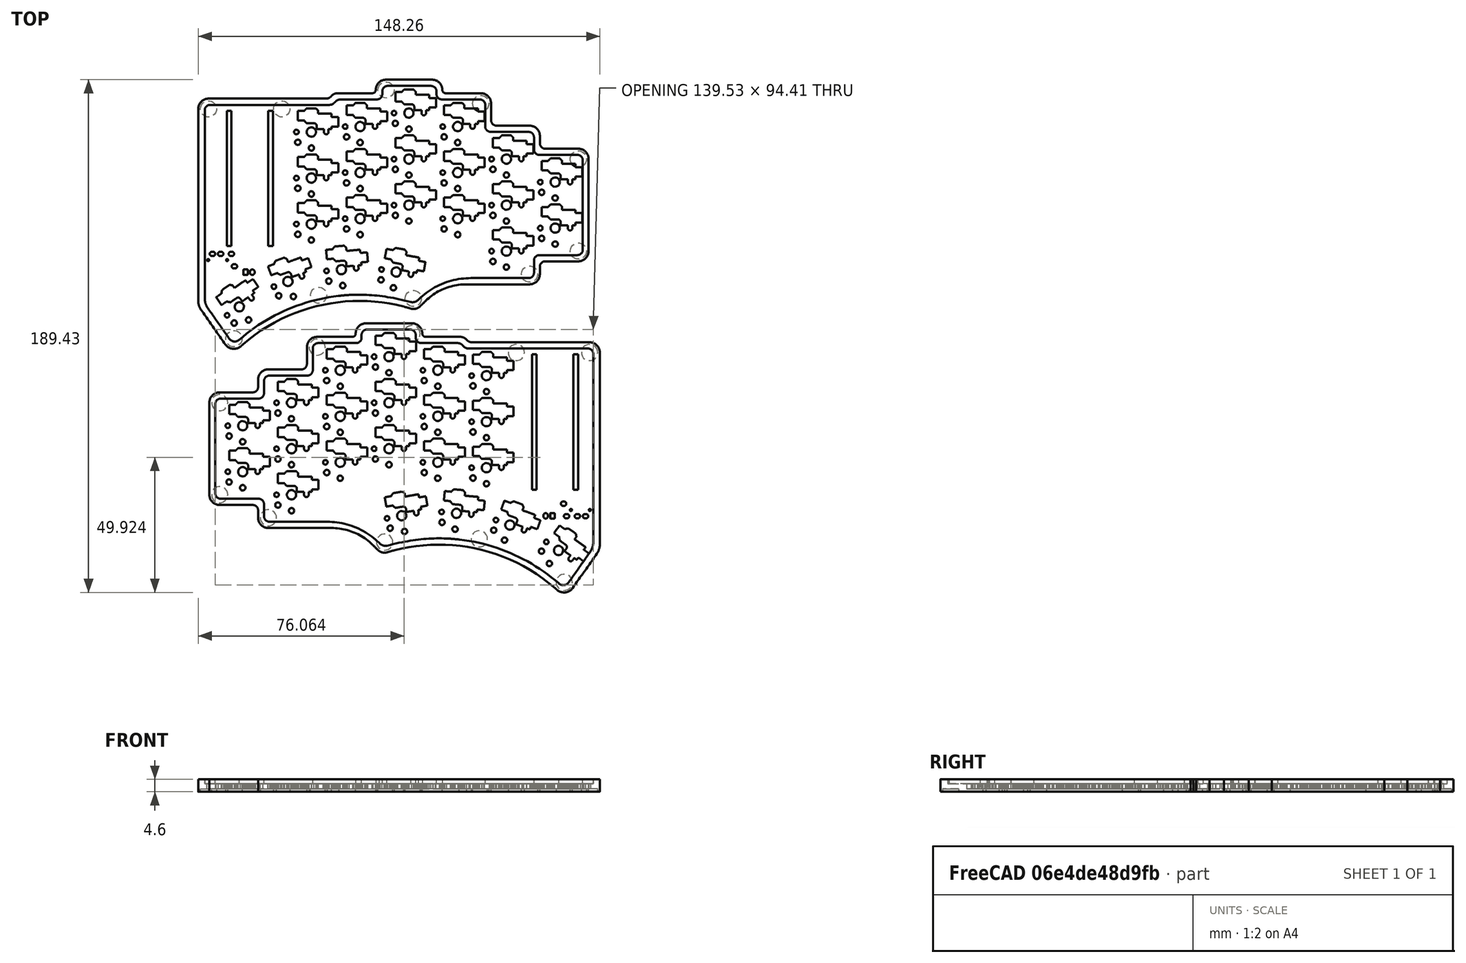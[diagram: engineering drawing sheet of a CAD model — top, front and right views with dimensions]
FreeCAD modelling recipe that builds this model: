
FCSTD DOCUMENT  (FreeCAD 0.21R33771 (Git))
Label: case_simple
License: All rights reserved
LicenseURL: http://en.wikipedia.org/wiki/All_rights_reserved
objects: Part::Feature×242, Part::Extrusion×242, Part::FeaturePython×5, Part::MultiFuse×3, Part::Mirroring×1
note: 493 computed .brp shape members not serialized (recipe doc carries the construction recipe); baked Part::Feature solids carry a one-line shape summary decoded from their .brp

FEATURE [Part::Feature] path44149_5_3
  shape: bbox 144.1 x 99.92 x 2e-07 mm, 0 faces, 0 solids (baked)
FEATURE [Part::Extrusion] Extrude  label="bounds"
  Base = -> path44149_5_3
  Dir = (0,0,1)
  DirMode = 0
  FaceMakerClass = Part::FaceMakerBullseye
  LengthFwd = 4.6
  LengthRev = 0
  Solid = true
  Symmetric = false
FEATURE [Part::Feature] path9
  Placement = pos=(72.4721,-86.7664,0) rot=(0,0,1;0rad)
  shape: bbox 6.624 x 7.244 x 2e-07 mm, 0 faces, 0 solids (baked)
FEATURE [Part::Feature] path9_9
  Placement = pos=(72.4721,-120.766,0) rot=(0,0,1;0rad)
  shape: bbox 6.624 x 7.244 x 2e-07 mm, 0 faces, 0 solids (baked)
FEATURE [Part::Feature] path9_92_7_9_8
  Placement = pos=(108.472,-66.2664,0) rot=(0,0,1;0rad)
  shape: bbox 6.624 x 7.244 x 2e-07 mm, 0 faces, 0 solids (baked)
FEATURE [Part::Feature] path9_92_7_9_9
  Placement = pos=(143.472,-61.2664,0) rot=(0,0,1;0rad)
  shape: bbox 6.624 x 7.244 x 2e-07 mm, 0 faces, 0 solids (baked)
FEATURE [Part::Feature] path9_92_7_9_9_4
  Placement = pos=(209.001,-68.2664,0) rot=(0,0,1;0rad)
  shape: bbox 6.624 x 7.244 x 2e-07 mm, 0 faces, 0 solids (baked)
FEATURE [Part::Feature] path9_9_5
  Placement = pos=(90.4721,-129.266,0) rot=(0,0,1;0rad)
  shape: bbox 6.624 x 7.244 x 2e-07 mm, 0 faces, 0 solids (baked)
FEATURE [Part::Feature] path9_92_7_9_9_4_4_8_2
  Placement = pos=(199.634,-153.132,0) rot=(0,0,1;0rad)
  shape: bbox 6.624 x 7.244 x 2e-07 mm, 0 faces, 0 solids (baked)
FEATURE [Part::Feature] path9_92_7_9_9_4_4_8_2_4
  Placement = pos=(133.404,-138.274,0) rot=(0,0,1;0rad)
  shape: bbox 6.624 x 7.244 x 2e-07 mm, 0 faces, 0 solids (baked)
FEATURE [Part::Feature] path9_92_7_9_9_4_4_8_2_4_6
  Placement = pos=(168.299,-137.096,0) rot=(0,0,1;0rad)
  shape: bbox 6.624 x 7.244 x 2e-07 mm, 0 faces, 0 solids (baked)
FEATURE [Part::Feature] path9_92_7_9_9_4_4_8_2_4_0
  Placement = pos=(181.972,-68.2664,0) rot=(0,0,1;0rad)
  shape: bbox 6.624 x 7.244 x 2e-07 mm, 0 faces, 0 solids (baked)
FEATURE [Part::Extrusion] Extrude001
  Base = -> path9
  Dir = (0,0,1)
  DirMode = 0
  FaceMakerClass = Part::FaceMakerBullseye
  LengthFwd = 1
  LengthRev = 0
  Solid = true
  Symmetric = false
FEATURE [Part::Extrusion] Extrude002
  Base = -> path9_9
  Dir = (0,0,1)
  DirMode = 0
  FaceMakerClass = Part::FaceMakerBullseye
  LengthFwd = 1
  LengthRev = 0
  Solid = true
  Symmetric = false
FEATURE [Part::Extrusion] Extrude003
  Base = -> path9_92_7_9_8
  Dir = (0,0,1)
  DirMode = 0
  FaceMakerClass = Part::FaceMakerBullseye
  LengthFwd = 1
  LengthRev = 0
  Solid = true
  Symmetric = false
FEATURE [Part::Extrusion] Extrude004
  Base = -> path9_92_7_9_9
  Dir = (0,0,1)
  DirMode = 0
  FaceMakerClass = Part::FaceMakerBullseye
  LengthFwd = 1
  LengthRev = 0
  Solid = true
  Symmetric = false
FEATURE [Part::Extrusion] Extrude005
  Base = -> path9_92_7_9_9_4
  Dir = (0,0,1)
  DirMode = 0
  FaceMakerClass = Part::FaceMakerBullseye
  LengthFwd = 1
  LengthRev = 0
  Solid = true
  Symmetric = false
FEATURE [Part::Extrusion] Extrude006
  Base = -> path9_9_5
  Dir = (0,0,1)
  DirMode = 0
  FaceMakerClass = Part::FaceMakerBullseye
  LengthFwd = 1
  LengthRev = 0
  Solid = true
  Symmetric = false
FEATURE [Part::Extrusion] Extrude007
  Base = -> path9_92_7_9_9_4_4_8_2
  Dir = (0,0,1)
  DirMode = 0
  FaceMakerClass = Part::FaceMakerBullseye
  LengthFwd = 1
  LengthRev = 0
  Solid = true
  Symmetric = false
FEATURE [Part::Extrusion] Extrude008
  Base = -> path9_92_7_9_9_4_4_8_2_4
  Dir = (0,0,1)
  DirMode = 0
  FaceMakerClass = Part::FaceMakerBullseye
  LengthFwd = 1
  LengthRev = 0
  Solid = true
  Symmetric = false
FEATURE [Part::Extrusion] Extrude009
  Base = -> path9_92_7_9_9_4_4_8_2_4_6
  Dir = (0,0,1)
  DirMode = 0
  FaceMakerClass = Part::FaceMakerBullseye
  LengthFwd = 1
  LengthRev = 0
  Solid = true
  Symmetric = false
FEATURE [Part::Extrusion] Extrude010
  Base = -> path9_92_7_9_9_4_4_8_2_4_0
  Dir = (0,0,1)
  DirMode = 0
  FaceMakerClass = Part::FaceMakerBullseye
  LengthFwd = 1
  LengthRev = 0
  Solid = true
  Symmetric = false
FEATURE [Part::MultiFuse] Fusion  label="feet"
  Shapes = -> [Extrude010,Extrude001,Extrude002,Extrude003,Extrude004,Extrude005,Extrude006,Extrude007,Extrude008,Extrude009]
FEATURE [Part::Feature] path52377_0_5_0_4_2_41_0_0_5_6
  shape: bbox 15 x 9.586 x 2e-07 mm, 0 faces, 0 solids (baked)
FEATURE [Part::Feature] path34096_2_0
  Placement = pos=(15.9497,-145.166,0) rot=(0,0,1;0rad)
  shape: bbox 2.208 x 2.415 x 2e-07 mm, 0 faces, 0 solids (baked)
FEATURE [Part::Feature] path34096_9
  Placement = pos=(20.9497,-147.266,0) rot=(0,0,1;0rad)
  shape: bbox 2.208 x 2.415 x 2e-07 mm, 0 faces, 0 solids (baked)
FEATURE [Part::Feature] path34072_1_9
  Placement = pos=(15.4497,-141.366,0) rot=(0,0,1;0rad)
  shape: bbox 1.877 x 2.052 x 2e-07 mm, 0 faces, 0 solids (baked)
FEATURE [Part::Feature] path34070_8
  Placement = pos=(20.9497,-141.366,0) rot=(0,0,1;0rad)
  shape: bbox 3.787 x 4.141 x 2e-07 mm, 0 faces, 0 solids (baked)
FEATURE [Part::Feature] path52377_0_5_0_4_2_41_0_0_5_6_5
  shape: bbox 15 x 9.586 x 2e-07 mm, 0 faces, 0 solids (baked)
FEATURE [Part::Feature] path34096_2_0_4
  Placement = pos=(15.9497,-145.166,0) rot=(0,0,1;0rad)
  shape: bbox 2.208 x 2.415 x 2e-07 mm, 0 faces, 0 solids (baked)
FEATURE [Part::Feature] path34096_9_4
  Placement = pos=(20.9497,-147.266,0) rot=(0,0,1;0rad)
  shape: bbox 2.208 x 2.415 x 2e-07 mm, 0 faces, 0 solids (baked)
FEATURE [Part::Feature] path34072_1_9_5
  Placement = pos=(15.4497,-141.366,0) rot=(0,0,1;0rad)
  shape: bbox 1.877 x 2.052 x 2e-07 mm, 0 faces, 0 solids (baked)
FEATURE [Part::Feature] path34070_8_0
  Placement = pos=(20.9497,-141.366,0) rot=(0,0,1;0rad)
  shape: bbox 3.787 x 4.141 x 2e-07 mm, 0 faces, 0 solids (baked)
FEATURE [Part::Feature] path52377_0_5_0_4_2_41_0_0_5_6_1
  shape: bbox 15 x 9.586 x 2e-07 mm, 0 faces, 0 solids (baked)
FEATURE [Part::Feature] path34096_2_0_0
  Placement = pos=(15.9497,-145.166,0) rot=(0,0,1;0rad)
  shape: bbox 2.208 x 2.415 x 2e-07 mm, 0 faces, 0 solids (baked)
FEATURE [Part::Feature] path34096_9_5
  Placement = pos=(20.9497,-147.266,0) rot=(0,0,1;0rad)
  shape: bbox 2.208 x 2.415 x 2e-07 mm, 0 faces, 0 solids (baked)
FEATURE [Part::Feature] path34072_1_9_51
  Placement = pos=(15.4497,-141.366,0) rot=(0,0,1;0rad)
  shape: bbox 1.877 x 2.052 x 2e-07 mm, 0 faces, 0 solids (baked)
FEATURE [Part::Feature] path34070_8_4
  Placement = pos=(20.9497,-141.366,0) rot=(0,0,1;0rad)
  shape: bbox 3.787 x 4.141 x 2e-07 mm, 0 faces, 0 solids (baked)
FEATURE [Part::Feature] path52377_0_5_0_4_2_41_0_0_5_6_1_6
  shape: bbox 15 x 9.586 x 2e-07 mm, 0 faces, 0 solids (baked)
FEATURE [Part::Feature] path34096_2_0_0_2
  Placement = pos=(15.9497,-145.166,0) rot=(0,0,1;0rad)
  shape: bbox 2.208 x 2.415 x 2e-07 mm, 0 faces, 0 solids (baked)
FEATURE [Part::Feature] path34096_9_5_7
  Placement = pos=(20.9497,-147.266,0) rot=(0,0,1;0rad)
  shape: bbox 2.208 x 2.415 x 2e-07 mm, 0 faces, 0 solids (baked)
FEATURE [Part::Feature] path34072_1_9_51_2
  Placement = pos=(15.4497,-141.366,0) rot=(0,0,1;0rad)
  shape: bbox 1.877 x 2.052 x 2e-07 mm, 0 faces, 0 solids (baked)
FEATURE [Part::Feature] path34070_8_4_6
  Placement = pos=(20.9497,-141.366,0) rot=(0,0,1;0rad)
  shape: bbox 3.787 x 4.141 x 2e-07 mm, 0 faces, 0 solids (baked)
FEATURE [Part::Feature] path52377_0_5_0_4_2_41_0_0_5_6_5_7
  shape: bbox 15 x 9.586 x 2e-07 mm, 0 faces, 0 solids (baked)
FEATURE [Part::Feature] path34096_2_0_4_8
  Placement = pos=(15.9497,-145.166,0) rot=(0,0,1;0rad)
  shape: bbox 2.208 x 2.415 x 2e-07 mm, 0 faces, 0 solids (baked)
FEATURE [Part::Feature] path34096_9_4_8
  Placement = pos=(20.9497,-147.266,0) rot=(0,0,1;0rad)
  shape: bbox 2.208 x 2.415 x 2e-07 mm, 0 faces, 0 solids (baked)
FEATURE [Part::Feature] path34072_1_9_5_5
  Placement = pos=(15.4497,-141.366,0) rot=(0,0,1;0rad)
  shape: bbox 1.877 x 2.052 x 2e-07 mm, 0 faces, 0 solids (baked)
FEATURE [Part::Feature] path34070_8_0_8
  Placement = pos=(20.9497,-141.366,0) rot=(0,0,1;0rad)
  shape: bbox 3.787 x 4.141 x 2e-07 mm, 0 faces, 0 solids (baked)
FEATURE [Part::Feature] path52377_0_5_0_4_2_41_0_0_5_6_1_7
  shape: bbox 15 x 9.586 x 2e-07 mm, 0 faces, 0 solids (baked)
FEATURE [Part::Feature] path34096_2_0_0_4
  Placement = pos=(15.9497,-145.166,0) rot=(0,0,1;0rad)
  shape: bbox 2.208 x 2.415 x 2e-07 mm, 0 faces, 0 solids (baked)
FEATURE [Part::Feature] path34096_9_5_75
  Placement = pos=(20.9497,-147.266,0) rot=(0,0,1;0rad)
  shape: bbox 2.208 x 2.415 x 2e-07 mm, 0 faces, 0 solids (baked)
FEATURE [Part::Feature] path34072_1_9_51_8
  Placement = pos=(15.4497,-141.366,0) rot=(0,0,1;0rad)
  shape: bbox 1.877 x 2.052 x 2e-07 mm, 0 faces, 0 solids (baked)
FEATURE [Part::Feature] path34070_8_4_65
  Placement = pos=(20.9497,-141.366,0) rot=(0,0,1;0rad)
  shape: bbox 3.787 x 4.141 x 2e-07 mm, 0 faces, 0 solids (baked)
FEATURE [Part::Feature] path52377_0_5_0_4_2_41_0_0_5_6_1_6_5
  shape: bbox 15 x 9.586 x 2e-07 mm, 0 faces, 0 solids (baked)
FEATURE [Part::Feature] path34096_2_0_0_2_7
  Placement = pos=(15.9497,-145.166,0) rot=(0,0,1;0rad)
  shape: bbox 2.208 x 2.415 x 2e-07 mm, 0 faces, 0 solids (baked)
FEATURE [Part::Feature] path34096_9_5_7_9
  Placement = pos=(20.9497,-147.266,0) rot=(0,0,1;0rad)
  shape: bbox 2.208 x 2.415 x 2e-07 mm, 0 faces, 0 solids (baked)
FEATURE [Part::Feature] path34072_1_9_51_2_1
  Placement = pos=(15.4497,-141.366,0) rot=(0,0,1;0rad)
  shape: bbox 1.877 x 2.052 x 2e-07 mm, 0 faces, 0 solids (baked)
FEATURE [Part::Feature] path34070_8_4_6_1
  Placement = pos=(20.9497,-141.366,0) rot=(0,0,1;0rad)
  shape: bbox 3.787 x 4.141 x 2e-07 mm, 0 faces, 0 solids (baked)
FEATURE [Part::Feature] path52377_0_5_0_4_2_41_0_0_5_6_5_7_1
  shape: bbox 15 x 9.586 x 2e-07 mm, 0 faces, 0 solids (baked)
FEATURE [Part::Feature] path34096_2_0_4_8_5
  Placement = pos=(15.9497,-145.166,0) rot=(0,0,1;0rad)
  shape: bbox 2.208 x 2.415 x 2e-07 mm, 0 faces, 0 solids (baked)
FEATURE [Part::Feature] path34096_9_4_8_5
  Placement = pos=(20.9497,-147.266,0) rot=(0,0,1;0rad)
  shape: bbox 2.208 x 2.415 x 2e-07 mm, 0 faces, 0 solids (baked)
FEATURE [Part::Feature] path34072_1_9_5_5_4
  Placement = pos=(15.4497,-141.366,0) rot=(0,0,1;0rad)
  shape: bbox 1.877 x 2.052 x 2e-07 mm, 0 faces, 0 solids (baked)
FEATURE [Part::Feature] path34070_8_0_8_3
  Placement = pos=(20.9497,-141.366,0) rot=(0,0,1;0rad)
  shape: bbox 3.787 x 4.141 x 2e-07 mm, 0 faces, 0 solids (baked)
FEATURE [Part::Feature] path52377_0_5_0_4_2_41_0_0_5_6_1_7_8
  shape: bbox 15 x 9.586 x 2e-07 mm, 0 faces, 0 solids (baked)
FEATURE [Part::Feature] path34096_2_0_0_4_5
  Placement = pos=(15.9497,-145.166,0) rot=(0,0,1;0rad)
  shape: bbox 2.208 x 2.415 x 2e-07 mm, 0 faces, 0 solids (baked)
FEATURE [Part::Feature] path34096_9_5_75_5
  Placement = pos=(20.9497,-147.266,0) rot=(0,0,1;0rad)
  shape: bbox 2.208 x 2.415 x 2e-07 mm, 0 faces, 0 solids (baked)
FEATURE [Part::Feature] path34072_1_9_51_8_1
  Placement = pos=(15.4497,-141.366,0) rot=(0,0,1;0rad)
  shape: bbox 1.877 x 2.052 x 2e-07 mm, 0 faces, 0 solids (baked)
FEATURE [Part::Feature] path34070_8_4_65_1
  Placement = pos=(20.9497,-141.366,0) rot=(0,0,1;0rad)
  shape: bbox 3.787 x 4.141 x 2e-07 mm, 0 faces, 0 solids (baked)
FEATURE [Part::Feature] path52377_0_5_0_4_2_41_0_0_5_6_1_6_5_2
  shape: bbox 15 x 9.586 x 2e-07 mm, 0 faces, 0 solids (baked)
FEATURE [Part::Feature] path34096_2_0_0_2_7_9
  Placement = pos=(15.9497,-145.166,0) rot=(0,0,1;0rad)
  shape: bbox 2.208 x 2.415 x 2e-07 mm, 0 faces, 0 solids (baked)
FEATURE [Part::Feature] path34096_9_5_7_9_4
  Placement = pos=(20.9497,-147.266,0) rot=(0,0,1;0rad)
  shape: bbox 2.208 x 2.415 x 2e-07 mm, 0 faces, 0 solids (baked)
FEATURE [Part::Feature] path34072_1_9_51_2_1_3
  Placement = pos=(15.4497,-141.366,0) rot=(0,0,1;0rad)
  shape: bbox 1.877 x 2.052 x 2e-07 mm, 0 faces, 0 solids (baked)
FEATURE [Part::Feature] path34070_8_4_6_1_4
  Placement = pos=(20.9497,-141.366,0) rot=(0,0,1;0rad)
  shape: bbox 3.787 x 4.141 x 2e-07 mm, 0 faces, 0 solids (baked)
FEATURE [Part::Feature] path52377_0_5_0_4_2_41_0_0_5_6_5_7_1_6
  shape: bbox 15 x 9.586 x 2e-07 mm, 0 faces, 0 solids (baked)
FEATURE [Part::Feature] path34096_2_0_4_8_5_4
  Placement = pos=(15.9497,-145.166,0) rot=(0,0,1;0rad)
  shape: bbox 2.208 x 2.415 x 2e-07 mm, 0 faces, 0 solids (baked)
FEATURE [Part::Feature] path34096_9_4_8_5_3
  Placement = pos=(20.9497,-147.266,0) rot=(0,0,1;0rad)
  shape: bbox 2.208 x 2.415 x 2e-07 mm, 0 faces, 0 solids (baked)
FEATURE [Part::Feature] path34072_1_9_5_5_4_4
  Placement = pos=(15.4497,-141.366,0) rot=(0,0,1;0rad)
  shape: bbox 1.877 x 2.052 x 2e-07 mm, 0 faces, 0 solids (baked)
FEATURE [Part::Feature] path34070_8_0_8_3_3
  Placement = pos=(20.9497,-141.366,0) rot=(0,0,1;0rad)
  shape: bbox 3.787 x 4.141 x 2e-07 mm, 0 faces, 0 solids (baked)
FEATURE [Part::Feature] path52377_0_5_0_4_2_41_0_0_5_6_1_7_9
  shape: bbox 15 x 9.586 x 2e-07 mm, 0 faces, 0 solids (baked)
FEATURE [Part::Feature] path34096_2_0_0_4_52
  Placement = pos=(15.9497,-145.166,0) rot=(0,0,1;0rad)
  shape: bbox 2.208 x 2.415 x 2e-07 mm, 0 faces, 0 solids (baked)
FEATURE [Part::Feature] path34096_9_5_75_2
  Placement = pos=(20.9497,-147.266,0) rot=(0,0,1;0rad)
  shape: bbox 2.208 x 2.415 x 2e-07 mm, 0 faces, 0 solids (baked)
FEATURE [Part::Feature] path34072_1_9_51_8_2
  Placement = pos=(15.4497,-141.366,0) rot=(0,0,1;0rad)
  shape: bbox 1.877 x 2.052 x 2e-07 mm, 0 faces, 0 solids (baked)
FEATURE [Part::Feature] path34070_8_4_65_5
  Placement = pos=(20.9497,-141.366,0) rot=(0,0,1;0rad)
  shape: bbox 3.787 x 4.141 x 2e-07 mm, 0 faces, 0 solids (baked)
FEATURE [Part::Feature] path52377_0_5_0_4_2_41_0_0_5_6_1_6_5_3
  shape: bbox 15 x 9.586 x 2e-07 mm, 0 faces, 0 solids (baked)
FEATURE [Part::Feature] path34096_2_0_0_2_7_3
  Placement = pos=(15.9497,-145.166,0) rot=(0,0,1;0rad)
  shape: bbox 2.208 x 2.415 x 2e-07 mm, 0 faces, 0 solids (baked)
FEATURE [Part::Feature] path34096_9_5_7_9_0
  Placement = pos=(20.9497,-147.266,0) rot=(0,0,1;0rad)
  shape: bbox 2.208 x 2.415 x 2e-07 mm, 0 faces, 0 solids (baked)
FEATURE [Part::Feature] path34072_1_9_51_2_1_9
  Placement = pos=(15.4497,-141.366,0) rot=(0,0,1;0rad)
  shape: bbox 1.877 x 2.052 x 2e-07 mm, 0 faces, 0 solids (baked)
FEATURE [Part::Feature] path34070_8_4_6_1_5
  Placement = pos=(20.9497,-141.366,0) rot=(0,0,1;0rad)
  shape: bbox 3.787 x 4.141 x 2e-07 mm, 0 faces, 0 solids (baked)
FEATURE [Part::Feature] path52377_0_5_0_4_2_41_0_0_5_6_5_7_1_9
  shape: bbox 15 x 9.586 x 2e-07 mm, 0 faces, 0 solids (baked)
FEATURE [Part::Feature] path34096_2_0_4_8_5_1
  Placement = pos=(15.9497,-145.166,0) rot=(0,0,1;0rad)
  shape: bbox 2.208 x 2.415 x 2e-07 mm, 0 faces, 0 solids (baked)
FEATURE [Part::Feature] path34096_9_4_8_5_9
  Placement = pos=(20.9497,-147.266,0) rot=(0,0,1;0rad)
  shape: bbox 2.208 x 2.415 x 2e-07 mm, 0 faces, 0 solids (baked)
FEATURE [Part::Feature] path34072_1_9_5_5_4_3
  Placement = pos=(15.4497,-141.366,0) rot=(0,0,1;0rad)
  shape: bbox 1.877 x 2.052 x 2e-07 mm, 0 faces, 0 solids (baked)
FEATURE [Part::Feature] path34070_8_0_8_3_8
  Placement = pos=(20.9497,-141.366,0) rot=(0,0,1;0rad)
  shape: bbox 3.787 x 4.141 x 2e-07 mm, 0 faces, 0 solids (baked)
FEATURE [Part::Feature] path52377_0_5_0_4_2_41_0_0_5_6_5_7_1_9_7
  shape: bbox 15.77 x 8.879 x 2e-07 mm, 0 faces, 0 solids (baked)
FEATURE [Part::Feature] path34096_2_0_4_8_5_1_5
  Placement = pos=(15.9497,-145.166,0) rot=(0,0,1;0rad)
  shape: bbox 2.386 x 2.384 x 2e-07 mm, 0 faces, 0 solids (baked)
FEATURE [Part::Feature] path34096_9_4_8_5_9_9
  Placement = pos=(20.9497,-147.266,0) rot=(0,0,1;0rad)
  shape: bbox 2.386 x 2.384 x 2e-07 mm, 0 faces, 0 solids (baked)
FEATURE [Part::Feature] path34072_1_9_5_5_4_3_4
  Placement = pos=(15.4497,-141.366,0) rot=(0,0,1;0rad)
  shape: bbox 2.028 x 2.027 x 2e-07 mm, 0 faces, 0 solids (baked)
FEATURE [Part::Feature] path34070_8_0_8_3_8_5
  Placement = pos=(20.9497,-141.366,0) rot=(0,0,1;0rad)
  shape: bbox 4.091 x 4.089 x 2e-07 mm, 0 faces, 0 solids (baked)
FEATURE [Part::Feature] path52377_0_5_0_4_2_41_0_0_5_6_5_7_1_9_7_1
  shape: bbox 15.05 x 10.25 x 2e-07 mm, 0 faces, 0 solids (baked)
FEATURE [Part::Feature] path34096_2_0_4_8_5_1_5_0
  Placement = pos=(15.9497,-145.166,0) rot=(0,0,1;0rad)
  shape: bbox 2.351 x 2.407 x 2e-07 mm, 0 faces, 0 solids (baked)
FEATURE [Part::Feature] path34096_9_4_8_5_9_9_0
  Placement = pos=(20.9497,-147.266,0) rot=(0,0,1;0rad)
  shape: bbox 2.351 x 2.407 x 2e-07 mm, 0 faces, 0 solids (baked)
FEATURE [Part::Feature] path34072_1_9_5_5_4_3_4_2
  Placement = pos=(15.4497,-141.366,0) rot=(0,0,1;0rad)
  shape: bbox 1.999 x 2.046 x 2e-07 mm, 0 faces, 0 solids (baked)
FEATURE [Part::Feature] path34070_8_0_8_3_8_5_0
  Placement = pos=(20.9497,-141.366,0) rot=(0,0,1;0rad)
  shape: bbox 4.033 x 4.128 x 2e-07 mm, 0 faces, 0 solids (baked)
FEATURE [Part::Feature] path52377_0_5_0_4_2_41_0_0_5_6_5_7_1_9_7_1_9
  shape: bbox 14.52 x 11.86 x 2e-07 mm, 0 faces, 0 solids (baked)
FEATURE [Part::Feature] path34096_2_0_4_8_5_1_5_0_3
  Placement = pos=(15.9497,-145.166,0) rot=(0,0,1;0rad)
  shape: bbox 2.384 x 2.386 x 2e-07 mm, 0 faces, 0 solids (baked)
FEATURE [Part::Feature] path34096_9_4_8_5_9_9_0_4
  Placement = pos=(20.9497,-147.266,0) rot=(0,0,1;0rad)
  shape: bbox 2.384 x 2.386 x 2e-07 mm, 0 faces, 0 solids (baked)
FEATURE [Part::Feature] path34072_1_9_5_5_4_3_4_2_6
  Placement = pos=(15.4497,-141.366,0) rot=(0,0,1;0rad)
  shape: bbox 2.027 x 2.028 x 2e-07 mm, 0 faces, 0 solids (baked)
FEATURE [Part::Feature] path34070_8_0_8_3_8_5_0_4
  Placement = pos=(20.9497,-141.366,0) rot=(0,0,1;0rad)
  shape: bbox 4.089 x 4.091 x 2e-07 mm, 0 faces, 0 solids (baked)
FEATURE [Part::Feature] path52377_0_5_0_4_2_41_0_0_5_6_5_7_1_9_7_1_1
  shape: bbox 13 x 13.34 x 2e-07 mm, 0 faces, 0 solids (baked)
FEATURE [Part::Feature] path34096_2_0_4_8_5_1_5_0_5
  Placement = pos=(15.9497,-145.166,0) rot=(0,0,1;0rad)
  shape: bbox 2.407 x 2.351 x 2e-07 mm, 0 faces, 0 solids (baked)
FEATURE [Part::Feature] path34096_9_4_8_5_9_9_0_8
  Placement = pos=(20.9497,-147.266,0) rot=(0,0,1;0rad)
  shape: bbox 2.407 x 2.351 x 2e-07 mm, 0 faces, 0 solids (baked)
FEATURE [Part::Feature] path34072_1_9_5_5_4_3_4_2_3
  Placement = pos=(15.4497,-141.366,0) rot=(0,0,1;0rad)
  shape: bbox 2.046 x 1.999 x 2e-07 mm, 0 faces, 0 solids (baked)
FEATURE [Part::Feature] path34070_8_0_8_3_8_5_0_7
  Placement = pos=(20.9497,-141.366,0) rot=(0,0,1;0rad)
  shape: bbox 4.128 x 4.033 x 2e-07 mm, 0 faces, 0 solids (baked)
FEATURE [Part::Feature] path52377_0_5_0_4_2_41_0_0_5_6_1_7_0
  shape: bbox 15 x 9.586 x 2e-07 mm, 0 faces, 0 solids (baked)
FEATURE [Part::Feature] path34096_2_0_0_4_9
  Placement = pos=(15.9497,-145.166,0) rot=(0,0,1;0rad)
  shape: bbox 2.208 x 2.415 x 2e-07 mm, 0 faces, 0 solids (baked)
FEATURE [Part::Feature] path34096_9_5_75_3
  Placement = pos=(20.9497,-147.266,0) rot=(0,0,1;0rad)
  shape: bbox 2.208 x 2.415 x 2e-07 mm, 0 faces, 0 solids (baked)
FEATURE [Part::Feature] path34072_1_9_51_8_3
  Placement = pos=(15.4497,-141.366,0) rot=(0,0,1;0rad)
  shape: bbox 1.877 x 2.052 x 2e-07 mm, 0 faces, 0 solids (baked)
FEATURE [Part::Feature] path34070_8_4_65_6
  Placement = pos=(20.9497,-141.366,0) rot=(0,0,1;0rad)
  shape: bbox 3.787 x 4.141 x 2e-07 mm, 0 faces, 0 solids (baked)
FEATURE [Part::Feature] path52377_0_5_0_4_2_41_0_0_5_6_1_6_5_0
  shape: bbox 15 x 9.586 x 2e-07 mm, 0 faces, 0 solids (baked)
FEATURE [Part::Feature] path34096_2_0_0_2_7_5
  Placement = pos=(15.9497,-145.166,0) rot=(0,0,1;0rad)
  shape: bbox 2.208 x 2.415 x 2e-07 mm, 0 faces, 0 solids (baked)
FEATURE [Part::Feature] path34096_9_5_7_9_2
  Placement = pos=(20.9497,-147.266,0) rot=(0,0,1;0rad)
  shape: bbox 2.208 x 2.415 x 2e-07 mm, 0 faces, 0 solids (baked)
FEATURE [Part::Feature] path34072_1_9_51_2_1_4
  Placement = pos=(15.4497,-141.366,0) rot=(0,0,1;0rad)
  shape: bbox 1.877 x 2.052 x 2e-07 mm, 0 faces, 0 solids (baked)
FEATURE [Part::Feature] path34070_8_4_6_1_1
  Placement = pos=(20.9497,-141.366,0) rot=(0,0,1;0rad)
  shape: bbox 3.787 x 4.141 x 2e-07 mm, 0 faces, 0 solids (baked)
FEATURE [Part::Feature] path52377_0_5_0_4_2_41_0_0_5_6_5_7_1_3
  shape: bbox 15 x 9.586 x 2e-07 mm, 0 faces, 0 solids (baked)
FEATURE [Part::Feature] path34096_2_0_4_8_5_3
  Placement = pos=(15.9497,-145.166,0) rot=(0,0,1;0rad)
  shape: bbox 2.208 x 2.415 x 2e-07 mm, 0 faces, 0 solids (baked)
FEATURE [Part::Feature] path34096_9_4_8_5_8
  Placement = pos=(20.9497,-147.266,0) rot=(0,0,1;0rad)
  shape: bbox 2.208 x 2.415 x 2e-07 mm, 0 faces, 0 solids (baked)
FEATURE [Part::Feature] path34072_1_9_5_5_4_31
  Placement = pos=(15.4497,-141.366,0) rot=(0,0,1;0rad)
  shape: bbox 1.877 x 2.052 x 2e-07 mm, 0 faces, 0 solids (baked)
FEATURE [Part::Feature] path34070_8_0_8_3_1
  Placement = pos=(20.9497,-141.366,0) rot=(0,0,1;0rad)
  shape: bbox 3.787 x 4.141 x 2e-07 mm, 0 faces, 0 solids (baked)
FEATURE [Part::Feature] circle37307_9_0_7_1
  Placement = pos=(138.24,-66.7421,0) rot=(0,0,1;0rad)
  shape: bbox 0.8832 x 0.9658 x 2e-07 mm, 0 faces, 0 solids (baked)
FEATURE [Part::Feature] circle37313_0_5_2_6
  Placement = pos=(131.24,-66.7421,0) rot=(0,0,1;0rad)
  shape: bbox 0.8832 x 0.9658 x 2e-07 mm, 0 faces, 0 solids (baked)
FEATURE [Part::Feature] path8_2
  shape: bbox 2.002 x 1.601 x 2e-07 mm, 0 faces, 0 solids (baked)
FEATURE [Part::Feature] path4_1
  shape: bbox 2.002 x 1.601 x 2e-07 mm, 0 faces, 0 solids (baked)
FEATURE [Part::Feature] path6_5
  shape: bbox 2.002 x 1.601 x 2e-07 mm, 0 faces, 0 solids (baked)
FEATURE [Part::Feature] path2_5
  shape: bbox 2.002 x 1.601 x 2e-07 mm, 0 faces, 0 solids (baked)
FEATURE [Part::Feature] path37931_6_3_3
  shape: bbox 1.7 x 2 x 2e-07 mm, 0 faces, 0 solids (baked)
FEATURE [Part::Feature] path37937_8_1_8
  shape: bbox 1.702 x 2 x 2e-07 mm, 0 faces, 0 solids (baked)
FEATURE [Part::Feature] rect117948_1_5_1_8
  shape: bbox 1.7 x 49.96 x 2e-07 mm, 0 faces, 0 solids (baked)
FEATURE [Part::Feature] rect117948_2_0_8_5_8
  shape: bbox 1.7 x 49.96 x 2e-07 mm, 0 faces, 0 solids (baked)
FEATURE [Part::Extrusion] Extrude011
  Base = -> path52377_0_5_0_4_2_41_0_0_5_6
  Dir = (0,0,1)
  DirMode = 0
  FaceMakerClass = Part::FaceMakerBullseye
  LengthFwd = 2
  LengthRev = 0
  Solid = true
  Symmetric = false
FEATURE [Part::Extrusion] Extrude012
  Base = -> path34096_2_0
  Dir = (0,0,1)
  DirMode = 0
  FaceMakerClass = Part::FaceMakerBullseye
  LengthFwd = 2
  LengthRev = 0
  Solid = true
  Symmetric = false
FEATURE [Part::Extrusion] Extrude013
  Base = -> path34096_9
  Dir = (0,0,1)
  DirMode = 0
  FaceMakerClass = Part::FaceMakerBullseye
  LengthFwd = 2
  LengthRev = 0
  Solid = true
  Symmetric = false
FEATURE [Part::Extrusion] Extrude014
  Base = -> path34072_1_9
  Dir = (0,0,1)
  DirMode = 0
  FaceMakerClass = Part::FaceMakerBullseye
  LengthFwd = 2
  LengthRev = 0
  Solid = true
  Symmetric = false
FEATURE [Part::Extrusion] Extrude015
  Base = -> path34070_8
  Dir = (0,0,1)
  DirMode = 0
  FaceMakerClass = Part::FaceMakerBullseye
  LengthFwd = 2
  LengthRev = 0
  Solid = true
  Symmetric = false
FEATURE [Part::Extrusion] Extrude016
  Base = -> path52377_0_5_0_4_2_41_0_0_5_6_5
  Dir = (0,0,1)
  DirMode = 0
  FaceMakerClass = Part::FaceMakerBullseye
  LengthFwd = 2
  LengthRev = 0
  Solid = true
  Symmetric = false
FEATURE [Part::Extrusion] Extrude017
  Base = -> path34096_2_0_4
  Dir = (0,0,1)
  DirMode = 0
  FaceMakerClass = Part::FaceMakerBullseye
  LengthFwd = 2
  LengthRev = 0
  Solid = true
  Symmetric = false
FEATURE [Part::Extrusion] Extrude018
  Base = -> path34096_9_4
  Dir = (0,0,1)
  DirMode = 0
  FaceMakerClass = Part::FaceMakerBullseye
  LengthFwd = 2
  LengthRev = 0
  Solid = true
  Symmetric = false
FEATURE [Part::Extrusion] Extrude019
  Base = -> path34072_1_9_5
  Dir = (0,0,1)
  DirMode = 0
  FaceMakerClass = Part::FaceMakerBullseye
  LengthFwd = 2
  LengthRev = 0
  Solid = true
  Symmetric = false
FEATURE [Part::Extrusion] Extrude020
  Base = -> path34070_8_0
  Dir = (0,0,1)
  DirMode = 0
  FaceMakerClass = Part::FaceMakerBullseye
  LengthFwd = 2
  LengthRev = 0
  Solid = true
  Symmetric = false
FEATURE [Part::Extrusion] Extrude021
  Base = -> path52377_0_5_0_4_2_41_0_0_5_6_1
  Dir = (0,0,1)
  DirMode = 0
  FaceMakerClass = Part::FaceMakerBullseye
  LengthFwd = 2
  LengthRev = 0
  Solid = true
  Symmetric = false
FEATURE [Part::Extrusion] Extrude022
  Base = -> path34096_2_0_0
  Dir = (0,0,1)
  DirMode = 0
  FaceMakerClass = Part::FaceMakerBullseye
  LengthFwd = 2
  LengthRev = 0
  Solid = true
  Symmetric = false
FEATURE [Part::Extrusion] Extrude023
  Base = -> path34096_9_5
  Dir = (0,0,1)
  DirMode = 0
  FaceMakerClass = Part::FaceMakerBullseye
  LengthFwd = 2
  LengthRev = 0
  Solid = true
  Symmetric = false
FEATURE [Part::Extrusion] Extrude024
  Base = -> path34072_1_9_51
  Dir = (0,0,1)
  DirMode = 0
  FaceMakerClass = Part::FaceMakerBullseye
  LengthFwd = 2
  LengthRev = 0
  Solid = true
  Symmetric = false
FEATURE [Part::Extrusion] Extrude025
  Base = -> path34070_8_4
  Dir = (0,0,1)
  DirMode = 0
  FaceMakerClass = Part::FaceMakerBullseye
  LengthFwd = 2
  LengthRev = 0
  Solid = true
  Symmetric = false
FEATURE [Part::Extrusion] Extrude026
  Base = -> path52377_0_5_0_4_2_41_0_0_5_6_1_6
  Dir = (0,0,1)
  DirMode = 0
  FaceMakerClass = Part::FaceMakerBullseye
  LengthFwd = 2
  LengthRev = 0
  Solid = true
  Symmetric = false
FEATURE [Part::Extrusion] Extrude027
  Base = -> path34096_2_0_0_2
  Dir = (0,0,1)
  DirMode = 0
  FaceMakerClass = Part::FaceMakerBullseye
  LengthFwd = 2
  LengthRev = 0
  Solid = true
  Symmetric = false
FEATURE [Part::Extrusion] Extrude028
  Base = -> path34096_9_5_7
  Dir = (0,0,1)
  DirMode = 0
  FaceMakerClass = Part::FaceMakerBullseye
  LengthFwd = 2
  LengthRev = 0
  Solid = true
  Symmetric = false
FEATURE [Part::Extrusion] Extrude029
  Base = -> path34072_1_9_51_2
  Dir = (0,0,1)
  DirMode = 0
  FaceMakerClass = Part::FaceMakerBullseye
  LengthFwd = 2
  LengthRev = 0
  Solid = true
  Symmetric = false
FEATURE [Part::Extrusion] Extrude030
  Base = -> path34070_8_4_6
  Dir = (0,0,1)
  DirMode = 0
  FaceMakerClass = Part::FaceMakerBullseye
  LengthFwd = 2
  LengthRev = 0
  Solid = true
  Symmetric = false
FEATURE [Part::Extrusion] Extrude031
  Base = -> path52377_0_5_0_4_2_41_0_0_5_6_5_7
  Dir = (0,0,1)
  DirMode = 0
  FaceMakerClass = Part::FaceMakerBullseye
  LengthFwd = 2
  LengthRev = 0
  Solid = true
  Symmetric = false
FEATURE [Part::Extrusion] Extrude032
  Base = -> path34096_2_0_4_8
  Dir = (0,0,1)
  DirMode = 0
  FaceMakerClass = Part::FaceMakerBullseye
  LengthFwd = 2
  LengthRev = 0
  Solid = true
  Symmetric = false
FEATURE [Part::Extrusion] Extrude033
  Base = -> path34096_9_4_8
  Dir = (0,0,1)
  DirMode = 0
  FaceMakerClass = Part::FaceMakerBullseye
  LengthFwd = 2
  LengthRev = 0
  Solid = true
  Symmetric = false
FEATURE [Part::Extrusion] Extrude034
  Base = -> path34072_1_9_5_5
  Dir = (0,0,1)
  DirMode = 0
  FaceMakerClass = Part::FaceMakerBullseye
  LengthFwd = 2
  LengthRev = 0
  Solid = true
  Symmetric = false
FEATURE [Part::Extrusion] Extrude035
  Base = -> path34070_8_0_8
  Dir = (0,0,1)
  DirMode = 0
  FaceMakerClass = Part::FaceMakerBullseye
  LengthFwd = 2
  LengthRev = 0
  Solid = true
  Symmetric = false
FEATURE [Part::Extrusion] Extrude036
  Base = -> path52377_0_5_0_4_2_41_0_0_5_6_1_7
  Dir = (0,0,1)
  DirMode = 0
  FaceMakerClass = Part::FaceMakerBullseye
  LengthFwd = 2
  LengthRev = 0
  Solid = true
  Symmetric = false
FEATURE [Part::Extrusion] Extrude037
  Base = -> path34096_2_0_0_4
  Dir = (0,0,1)
  DirMode = 0
  FaceMakerClass = Part::FaceMakerBullseye
  LengthFwd = 2
  LengthRev = 0
  Solid = true
  Symmetric = false
FEATURE [Part::Extrusion] Extrude038
  Base = -> path34096_9_5_75
  Dir = (0,0,1)
  DirMode = 0
  FaceMakerClass = Part::FaceMakerBullseye
  LengthFwd = 2
  LengthRev = 0
  Solid = true
  Symmetric = false
FEATURE [Part::Extrusion] Extrude039
  Base = -> path34072_1_9_51_8
  Dir = (0,0,1)
  DirMode = 0
  FaceMakerClass = Part::FaceMakerBullseye
  LengthFwd = 2
  LengthRev = 0
  Solid = true
  Symmetric = false
FEATURE [Part::Extrusion] Extrude040
  Base = -> path34070_8_4_65
  Dir = (0,0,1)
  DirMode = 0
  FaceMakerClass = Part::FaceMakerBullseye
  LengthFwd = 2
  LengthRev = 0
  Solid = true
  Symmetric = false
FEATURE [Part::Extrusion] Extrude041
  Base = -> path52377_0_5_0_4_2_41_0_0_5_6_1_6_5
  Dir = (0,0,1)
  DirMode = 0
  FaceMakerClass = Part::FaceMakerBullseye
  LengthFwd = 2
  LengthRev = 0
  Solid = true
  Symmetric = false
FEATURE [Part::Extrusion] Extrude042
  Base = -> path34096_2_0_0_2_7
  Dir = (0,0,1)
  DirMode = 0
  FaceMakerClass = Part::FaceMakerBullseye
  LengthFwd = 2
  LengthRev = 0
  Solid = true
  Symmetric = false
FEATURE [Part::Extrusion] Extrude043
  Base = -> path34096_9_5_7_9
  Dir = (0,0,1)
  DirMode = 0
  FaceMakerClass = Part::FaceMakerBullseye
  LengthFwd = 2
  LengthRev = 0
  Solid = true
  Symmetric = false
FEATURE [Part::Extrusion] Extrude044
  Base = -> path34072_1_9_51_2_1
  Dir = (0,0,1)
  DirMode = 0
  FaceMakerClass = Part::FaceMakerBullseye
  LengthFwd = 2
  LengthRev = 0
  Solid = true
  Symmetric = false
FEATURE [Part::Extrusion] Extrude045
  Base = -> path34070_8_4_6_1
  Dir = (0,0,1)
  DirMode = 0
  FaceMakerClass = Part::FaceMakerBullseye
  LengthFwd = 2
  LengthRev = 0
  Solid = true
  Symmetric = false
FEATURE [Part::Extrusion] Extrude046
  Base = -> path52377_0_5_0_4_2_41_0_0_5_6_5_7_1
  Dir = (0,0,1)
  DirMode = 0
  FaceMakerClass = Part::FaceMakerBullseye
  LengthFwd = 2
  LengthRev = 0
  Solid = true
  Symmetric = false
FEATURE [Part::Extrusion] Extrude047
  Base = -> path34096_2_0_4_8_5
  Dir = (0,0,1)
  DirMode = 0
  FaceMakerClass = Part::FaceMakerBullseye
  LengthFwd = 2
  LengthRev = 0
  Solid = true
  Symmetric = false
FEATURE [Part::Extrusion] Extrude048
  Base = -> path34096_9_4_8_5
  Dir = (0,0,1)
  DirMode = 0
  FaceMakerClass = Part::FaceMakerBullseye
  LengthFwd = 2
  LengthRev = 0
  Solid = true
  Symmetric = false
FEATURE [Part::Extrusion] Extrude049
  Base = -> path34072_1_9_5_5_4
  Dir = (0,0,1)
  DirMode = 0
  FaceMakerClass = Part::FaceMakerBullseye
  LengthFwd = 2
  LengthRev = 0
  Solid = true
  Symmetric = false
FEATURE [Part::Extrusion] Extrude050
  Base = -> path34070_8_0_8_3
  Dir = (0,0,1)
  DirMode = 0
  FaceMakerClass = Part::FaceMakerBullseye
  LengthFwd = 2
  LengthRev = 0
  Solid = true
  Symmetric = false
FEATURE [Part::Extrusion] Extrude051
  Base = -> path52377_0_5_0_4_2_41_0_0_5_6_1_7_8
  Dir = (0,0,1)
  DirMode = 0
  FaceMakerClass = Part::FaceMakerBullseye
  LengthFwd = 2
  LengthRev = 0
  Solid = true
  Symmetric = false
FEATURE [Part::Extrusion] Extrude052
  Base = -> path34096_2_0_0_4_5
  Dir = (0,0,1)
  DirMode = 0
  FaceMakerClass = Part::FaceMakerBullseye
  LengthFwd = 2
  LengthRev = 0
  Solid = true
  Symmetric = false
FEATURE [Part::Extrusion] Extrude053
  Base = -> path34096_9_5_75_5
  Dir = (0,0,1)
  DirMode = 0
  FaceMakerClass = Part::FaceMakerBullseye
  LengthFwd = 2
  LengthRev = 0
  Solid = true
  Symmetric = false
FEATURE [Part::Extrusion] Extrude054
  Base = -> path34072_1_9_51_8_1
  Dir = (0,0,1)
  DirMode = 0
  FaceMakerClass = Part::FaceMakerBullseye
  LengthFwd = 2
  LengthRev = 0
  Solid = true
  Symmetric = false
FEATURE [Part::Extrusion] Extrude055
  Base = -> path34070_8_4_65_1
  Dir = (0,0,1)
  DirMode = 0
  FaceMakerClass = Part::FaceMakerBullseye
  LengthFwd = 2
  LengthRev = 0
  Solid = true
  Symmetric = false
FEATURE [Part::Extrusion] Extrude056
  Base = -> path52377_0_5_0_4_2_41_0_0_5_6_1_6_5_2
  Dir = (0,0,1)
  DirMode = 0
  FaceMakerClass = Part::FaceMakerBullseye
  LengthFwd = 2
  LengthRev = 0
  Solid = true
  Symmetric = false
FEATURE [Part::Extrusion] Extrude057
  Base = -> path34096_2_0_0_2_7_9
  Dir = (0,0,1)
  DirMode = 0
  FaceMakerClass = Part::FaceMakerBullseye
  LengthFwd = 2
  LengthRev = 0
  Solid = true
  Symmetric = false
FEATURE [Part::Extrusion] Extrude058
  Base = -> path34096_9_5_7_9_4
  Dir = (0,0,1)
  DirMode = 0
  FaceMakerClass = Part::FaceMakerBullseye
  LengthFwd = 2
  LengthRev = 0
  Solid = true
  Symmetric = false
FEATURE [Part::Extrusion] Extrude059
  Base = -> path34072_1_9_51_2_1_3
  Dir = (0,0,1)
  DirMode = 0
  FaceMakerClass = Part::FaceMakerBullseye
  LengthFwd = 2
  LengthRev = 0
  Solid = true
  Symmetric = false
FEATURE [Part::Extrusion] Extrude060
  Base = -> path34070_8_4_6_1_4
  Dir = (0,0,1)
  DirMode = 0
  FaceMakerClass = Part::FaceMakerBullseye
  LengthFwd = 2
  LengthRev = 0
  Solid = true
  Symmetric = false
FEATURE [Part::Extrusion] Extrude061
  Base = -> path52377_0_5_0_4_2_41_0_0_5_6_5_7_1_6
  Dir = (0,0,1)
  DirMode = 0
  FaceMakerClass = Part::FaceMakerBullseye
  LengthFwd = 2
  LengthRev = 0
  Solid = true
  Symmetric = false
FEATURE [Part::Extrusion] Extrude062
  Base = -> path34096_2_0_4_8_5_4
  Dir = (0,0,1)
  DirMode = 0
  FaceMakerClass = Part::FaceMakerBullseye
  LengthFwd = 2
  LengthRev = 0
  Solid = true
  Symmetric = false
FEATURE [Part::Extrusion] Extrude063
  Base = -> path34096_9_4_8_5_3
  Dir = (0,0,1)
  DirMode = 0
  FaceMakerClass = Part::FaceMakerBullseye
  LengthFwd = 2
  LengthRev = 0
  Solid = true
  Symmetric = false
FEATURE [Part::Extrusion] Extrude064
  Base = -> path34072_1_9_5_5_4_4
  Dir = (0,0,1)
  DirMode = 0
  FaceMakerClass = Part::FaceMakerBullseye
  LengthFwd = 2
  LengthRev = 0
  Solid = true
  Symmetric = false
FEATURE [Part::Extrusion] Extrude065
  Base = -> path34070_8_0_8_3_3
  Dir = (0,0,1)
  DirMode = 0
  FaceMakerClass = Part::FaceMakerBullseye
  LengthFwd = 2
  LengthRev = 0
  Solid = true
  Symmetric = false
FEATURE [Part::Extrusion] Extrude066
  Base = -> path52377_0_5_0_4_2_41_0_0_5_6_1_7_9
  Dir = (0,0,1)
  DirMode = 0
  FaceMakerClass = Part::FaceMakerBullseye
  LengthFwd = 2
  LengthRev = 0
  Solid = true
  Symmetric = false
FEATURE [Part::Extrusion] Extrude067
  Base = -> path34096_2_0_0_4_52
  Dir = (0,0,1)
  DirMode = 0
  FaceMakerClass = Part::FaceMakerBullseye
  LengthFwd = 2
  LengthRev = 0
  Solid = true
  Symmetric = false
FEATURE [Part::Extrusion] Extrude068
  Base = -> path34096_9_5_75_2
  Dir = (0,0,1)
  DirMode = 0
  FaceMakerClass = Part::FaceMakerBullseye
  LengthFwd = 2
  LengthRev = 0
  Solid = true
  Symmetric = false
FEATURE [Part::Extrusion] Extrude069
  Base = -> path34072_1_9_51_8_2
  Dir = (0,0,1)
  DirMode = 0
  FaceMakerClass = Part::FaceMakerBullseye
  LengthFwd = 2
  LengthRev = 0
  Solid = true
  Symmetric = false
FEATURE [Part::Extrusion] Extrude070
  Base = -> path34070_8_4_65_5
  Dir = (0,0,1)
  DirMode = 0
  FaceMakerClass = Part::FaceMakerBullseye
  LengthFwd = 2
  LengthRev = 0
  Solid = true
  Symmetric = false
FEATURE [Part::Extrusion] Extrude071
  Base = -> path52377_0_5_0_4_2_41_0_0_5_6_1_6_5_3
  Dir = (0,0,1)
  DirMode = 0
  FaceMakerClass = Part::FaceMakerBullseye
  LengthFwd = 2
  LengthRev = 0
  Solid = true
  Symmetric = false
FEATURE [Part::Extrusion] Extrude072
  Base = -> path34096_2_0_0_2_7_3
  Dir = (0,0,1)
  DirMode = 0
  FaceMakerClass = Part::FaceMakerBullseye
  LengthFwd = 2
  LengthRev = 0
  Solid = true
  Symmetric = false
FEATURE [Part::Extrusion] Extrude073
  Base = -> path34096_9_5_7_9_0
  Dir = (0,0,1)
  DirMode = 0
  FaceMakerClass = Part::FaceMakerBullseye
  LengthFwd = 2
  LengthRev = 0
  Solid = true
  Symmetric = false
FEATURE [Part::Extrusion] Extrude074
  Base = -> path34072_1_9_51_2_1_9
  Dir = (0,0,1)
  DirMode = 0
  FaceMakerClass = Part::FaceMakerBullseye
  LengthFwd = 2
  LengthRev = 0
  Solid = true
  Symmetric = false
FEATURE [Part::Extrusion] Extrude075
  Base = -> path34070_8_4_6_1_5
  Dir = (0,0,1)
  DirMode = 0
  FaceMakerClass = Part::FaceMakerBullseye
  LengthFwd = 2
  LengthRev = 0
  Solid = true
  Symmetric = false
FEATURE [Part::Extrusion] Extrude076
  Base = -> path52377_0_5_0_4_2_41_0_0_5_6_5_7_1_9
  Dir = (0,0,1)
  DirMode = 0
  FaceMakerClass = Part::FaceMakerBullseye
  LengthFwd = 2
  LengthRev = 0
  Solid = true
  Symmetric = false
FEATURE [Part::Extrusion] Extrude077
  Base = -> path34096_2_0_4_8_5_1
  Dir = (0,0,1)
  DirMode = 0
  FaceMakerClass = Part::FaceMakerBullseye
  LengthFwd = 2
  LengthRev = 0
  Solid = true
  Symmetric = false
FEATURE [Part::Extrusion] Extrude078
  Base = -> path34096_9_4_8_5_9
  Dir = (0,0,1)
  DirMode = 0
  FaceMakerClass = Part::FaceMakerBullseye
  LengthFwd = 2
  LengthRev = 0
  Solid = true
  Symmetric = false
FEATURE [Part::Extrusion] Extrude079
  Base = -> path34072_1_9_5_5_4_3
  Dir = (0,0,1)
  DirMode = 0
  FaceMakerClass = Part::FaceMakerBullseye
  LengthFwd = 2
  LengthRev = 0
  Solid = true
  Symmetric = false
FEATURE [Part::Extrusion] Extrude080
  Base = -> path34070_8_0_8_3_8
  Dir = (0,0,1)
  DirMode = 0
  FaceMakerClass = Part::FaceMakerBullseye
  LengthFwd = 2
  LengthRev = 0
  Solid = true
  Symmetric = false
FEATURE [Part::Extrusion] Extrude081
  Base = -> path52377_0_5_0_4_2_41_0_0_5_6_5_7_1_9_7
  Dir = (0,0,1)
  DirMode = 0
  FaceMakerClass = Part::FaceMakerBullseye
  LengthFwd = 2
  LengthRev = 0
  Solid = true
  Symmetric = false
FEATURE [Part::Extrusion] Extrude082
  Base = -> path34096_2_0_4_8_5_1_5
  Dir = (0,0,1)
  DirMode = 0
  FaceMakerClass = Part::FaceMakerBullseye
  LengthFwd = 2
  LengthRev = 0
  Solid = true
  Symmetric = false
FEATURE [Part::Extrusion] Extrude083
  Base = -> path34096_9_4_8_5_9_9
  Dir = (0,0,1)
  DirMode = 0
  FaceMakerClass = Part::FaceMakerBullseye
  LengthFwd = 2
  LengthRev = 0
  Solid = true
  Symmetric = false
FEATURE [Part::Extrusion] Extrude084
  Base = -> path34072_1_9_5_5_4_3_4
  Dir = (0,0,1)
  DirMode = 0
  FaceMakerClass = Part::FaceMakerBullseye
  LengthFwd = 2
  LengthRev = 0
  Solid = true
  Symmetric = false
FEATURE [Part::Extrusion] Extrude085
  Base = -> path34070_8_0_8_3_8_5
  Dir = (0,0,1)
  DirMode = 0
  FaceMakerClass = Part::FaceMakerBullseye
  LengthFwd = 2
  LengthRev = 0
  Solid = true
  Symmetric = false
FEATURE [Part::Extrusion] Extrude086
  Base = -> path52377_0_5_0_4_2_41_0_0_5_6_5_7_1_9_7_1
  Dir = (0,0,1)
  DirMode = 0
  FaceMakerClass = Part::FaceMakerBullseye
  LengthFwd = 2
  LengthRev = 0
  Solid = true
  Symmetric = false
FEATURE [Part::Extrusion] Extrude087
  Base = -> path34096_2_0_4_8_5_1_5_0
  Dir = (0,0,1)
  DirMode = 0
  FaceMakerClass = Part::FaceMakerBullseye
  LengthFwd = 2
  LengthRev = 0
  Solid = true
  Symmetric = false
FEATURE [Part::Extrusion] Extrude088
  Base = -> path34096_9_4_8_5_9_9_0
  Dir = (0,0,1)
  DirMode = 0
  FaceMakerClass = Part::FaceMakerBullseye
  LengthFwd = 2
  LengthRev = 0
  Solid = true
  Symmetric = false
FEATURE [Part::Extrusion] Extrude089
  Base = -> path34072_1_9_5_5_4_3_4_2
  Dir = (0,0,1)
  DirMode = 0
  FaceMakerClass = Part::FaceMakerBullseye
  LengthFwd = 2
  LengthRev = 0
  Solid = true
  Symmetric = false
FEATURE [Part::Extrusion] Extrude090
  Base = -> path34070_8_0_8_3_8_5_0
  Dir = (0,0,1)
  DirMode = 0
  FaceMakerClass = Part::FaceMakerBullseye
  LengthFwd = 2
  LengthRev = 0
  Solid = true
  Symmetric = false
FEATURE [Part::Extrusion] Extrude091
  Base = -> path52377_0_5_0_4_2_41_0_0_5_6_5_7_1_9_7_1_9
  Dir = (0,0,1)
  DirMode = 0
  FaceMakerClass = Part::FaceMakerBullseye
  LengthFwd = 2
  LengthRev = 0
  Solid = true
  Symmetric = false
FEATURE [Part::Extrusion] Extrude092
  Base = -> path34096_2_0_4_8_5_1_5_0_3
  Dir = (0,0,1)
  DirMode = 0
  FaceMakerClass = Part::FaceMakerBullseye
  LengthFwd = 2
  LengthRev = 0
  Solid = true
  Symmetric = false
FEATURE [Part::Extrusion] Extrude093
  Base = -> path34096_9_4_8_5_9_9_0_4
  Dir = (0,0,1)
  DirMode = 0
  FaceMakerClass = Part::FaceMakerBullseye
  LengthFwd = 2
  LengthRev = 0
  Solid = true
  Symmetric = false
FEATURE [Part::Extrusion] Extrude094
  Base = -> path34072_1_9_5_5_4_3_4_2_6
  Dir = (0,0,1)
  DirMode = 0
  FaceMakerClass = Part::FaceMakerBullseye
  LengthFwd = 2
  LengthRev = 0
  Solid = true
  Symmetric = false
FEATURE [Part::Extrusion] Extrude095
  Base = -> path34070_8_0_8_3_8_5_0_4
  Dir = (0,0,1)
  DirMode = 0
  FaceMakerClass = Part::FaceMakerBullseye
  LengthFwd = 2
  LengthRev = 0
  Solid = true
  Symmetric = false
FEATURE [Part::Extrusion] Extrude096
  Base = -> path52377_0_5_0_4_2_41_0_0_5_6_5_7_1_9_7_1_1
  Dir = (0,0,1)
  DirMode = 0
  FaceMakerClass = Part::FaceMakerBullseye
  LengthFwd = 2
  LengthRev = 0
  Solid = true
  Symmetric = false
FEATURE [Part::Extrusion] Extrude097
  Base = -> path34096_2_0_4_8_5_1_5_0_5
  Dir = (0,0,1)
  DirMode = 0
  FaceMakerClass = Part::FaceMakerBullseye
  LengthFwd = 2
  LengthRev = 0
  Solid = true
  Symmetric = false
FEATURE [Part::Extrusion] Extrude098
  Base = -> path34096_9_4_8_5_9_9_0_8
  Dir = (0,0,1)
  DirMode = 0
  FaceMakerClass = Part::FaceMakerBullseye
  LengthFwd = 2
  LengthRev = 0
  Solid = true
  Symmetric = false
FEATURE [Part::Extrusion] Extrude099
  Base = -> path34072_1_9_5_5_4_3_4_2_3
  Dir = (0,0,1)
  DirMode = 0
  FaceMakerClass = Part::FaceMakerBullseye
  LengthFwd = 2
  LengthRev = 0
  Solid = true
  Symmetric = false
FEATURE [Part::Extrusion] Extrude100
  Base = -> path34070_8_0_8_3_8_5_0_7
  Dir = (0,0,1)
  DirMode = 0
  FaceMakerClass = Part::FaceMakerBullseye
  LengthFwd = 2
  LengthRev = 0
  Solid = true
  Symmetric = false
FEATURE [Part::Extrusion] Extrude101
  Base = -> path52377_0_5_0_4_2_41_0_0_5_6_1_7_0
  Dir = (0,0,1)
  DirMode = 0
  FaceMakerClass = Part::FaceMakerBullseye
  LengthFwd = 2
  LengthRev = 0
  Solid = true
  Symmetric = false
FEATURE [Part::Extrusion] Extrude102
  Base = -> path34096_2_0_0_4_9
  Dir = (0,0,1)
  DirMode = 0
  FaceMakerClass = Part::FaceMakerBullseye
  LengthFwd = 2
  LengthRev = 0
  Solid = true
  Symmetric = false
FEATURE [Part::Extrusion] Extrude103
  Base = -> path34096_9_5_75_3
  Dir = (0,0,1)
  DirMode = 0
  FaceMakerClass = Part::FaceMakerBullseye
  LengthFwd = 2
  LengthRev = 0
  Solid = true
  Symmetric = false
FEATURE [Part::Extrusion] Extrude104
  Base = -> path34072_1_9_51_8_3
  Dir = (0,0,1)
  DirMode = 0
  FaceMakerClass = Part::FaceMakerBullseye
  LengthFwd = 2
  LengthRev = 0
  Solid = true
  Symmetric = false
FEATURE [Part::Extrusion] Extrude105
  Base = -> path34070_8_4_65_6
  Dir = (0,0,1)
  DirMode = 0
  FaceMakerClass = Part::FaceMakerBullseye
  LengthFwd = 2
  LengthRev = 0
  Solid = true
  Symmetric = false
FEATURE [Part::Extrusion] Extrude106
  Base = -> path52377_0_5_0_4_2_41_0_0_5_6_1_6_5_0
  Dir = (0,0,1)
  DirMode = 0
  FaceMakerClass = Part::FaceMakerBullseye
  LengthFwd = 2
  LengthRev = 0
  Solid = true
  Symmetric = false
FEATURE [Part::Extrusion] Extrude107
  Base = -> path34096_2_0_0_2_7_5
  Dir = (0,0,1)
  DirMode = 0
  FaceMakerClass = Part::FaceMakerBullseye
  LengthFwd = 2
  LengthRev = 0
  Solid = true
  Symmetric = false
FEATURE [Part::Extrusion] Extrude108
  Base = -> path34096_9_5_7_9_2
  Dir = (0,0,1)
  DirMode = 0
  FaceMakerClass = Part::FaceMakerBullseye
  LengthFwd = 2
  LengthRev = 0
  Solid = true
  Symmetric = false
FEATURE [Part::Extrusion] Extrude109
  Base = -> path34072_1_9_51_2_1_4
  Dir = (0,0,1)
  DirMode = 0
  FaceMakerClass = Part::FaceMakerBullseye
  LengthFwd = 2
  LengthRev = 0
  Solid = true
  Symmetric = false
FEATURE [Part::Extrusion] Extrude110
  Base = -> path34070_8_4_6_1_1
  Dir = (0,0,1)
  DirMode = 0
  FaceMakerClass = Part::FaceMakerBullseye
  LengthFwd = 2
  LengthRev = 0
  Solid = true
  Symmetric = false
FEATURE [Part::Extrusion] Extrude111
  Base = -> path52377_0_5_0_4_2_41_0_0_5_6_5_7_1_3
  Dir = (0,0,1)
  DirMode = 0
  FaceMakerClass = Part::FaceMakerBullseye
  LengthFwd = 2
  LengthRev = 0
  Solid = true
  Symmetric = false
FEATURE [Part::Extrusion] Extrude112
  Base = -> path34096_2_0_4_8_5_3
  Dir = (0,0,1)
  DirMode = 0
  FaceMakerClass = Part::FaceMakerBullseye
  LengthFwd = 2
  LengthRev = 0
  Solid = true
  Symmetric = false
FEATURE [Part::Extrusion] Extrude113
  Base = -> path34096_9_4_8_5_8
  Dir = (0,0,1)
  DirMode = 0
  FaceMakerClass = Part::FaceMakerBullseye
  LengthFwd = 2
  LengthRev = 0
  Solid = true
  Symmetric = false
FEATURE [Part::Extrusion] Extrude114
  Base = -> path34072_1_9_5_5_4_31
  Dir = (0,0,1)
  DirMode = 0
  FaceMakerClass = Part::FaceMakerBullseye
  LengthFwd = 2
  LengthRev = 0
  Solid = true
  Symmetric = false
FEATURE [Part::Extrusion] Extrude115
  Base = -> path34070_8_0_8_3_1
  Dir = (0,0,1)
  DirMode = 0
  FaceMakerClass = Part::FaceMakerBullseye
  LengthFwd = 2
  LengthRev = 0
  Solid = true
  Symmetric = false
FEATURE [Part::Extrusion] Extrude116
  Base = -> circle37307_9_0_7_1
  Dir = (0,0,1)
  DirMode = 0
  FaceMakerClass = Part::FaceMakerBullseye
  LengthFwd = 2
  LengthRev = 0
  Solid = true
  Symmetric = false
FEATURE [Part::Extrusion] Extrude117
  Base = -> circle37313_0_5_2_6
  Dir = (0,0,1)
  DirMode = 0
  FaceMakerClass = Part::FaceMakerBullseye
  LengthFwd = 2
  LengthRev = 0
  Solid = true
  Symmetric = false
FEATURE [Part::Extrusion] Extrude118
  Base = -> path8_2
  Dir = (0,0,1)
  DirMode = 0
  FaceMakerClass = Part::FaceMakerBullseye
  LengthFwd = 2
  LengthRev = 0
  Solid = true
  Symmetric = false
FEATURE [Part::Extrusion] Extrude119
  Base = -> path4_1
  Dir = (0,0,1)
  DirMode = 0
  FaceMakerClass = Part::FaceMakerBullseye
  LengthFwd = 2
  LengthRev = 0
  Solid = true
  Symmetric = false
FEATURE [Part::Extrusion] Extrude120
  Base = -> path6_5
  Dir = (0,0,1)
  DirMode = 0
  FaceMakerClass = Part::FaceMakerBullseye
  LengthFwd = 2
  LengthRev = 0
  Solid = true
  Symmetric = false
FEATURE [Part::Extrusion] Extrude121
  Base = -> path2_5
  Dir = (0,0,1)
  DirMode = 0
  FaceMakerClass = Part::FaceMakerBullseye
  LengthFwd = 2
  LengthRev = 0
  Solid = true
  Symmetric = false
FEATURE [Part::Extrusion] Extrude122
  Base = -> path37931_6_3_3
  Dir = (0,0,1)
  DirMode = 0
  FaceMakerClass = Part::FaceMakerBullseye
  LengthFwd = 2
  LengthRev = 0
  Solid = true
  Symmetric = false
FEATURE [Part::Extrusion] Extrude123
  Base = -> path37937_8_1_8
  Dir = (0,0,1)
  DirMode = 0
  FaceMakerClass = Part::FaceMakerBullseye
  LengthFwd = 2
  LengthRev = 0
  Solid = true
  Symmetric = false
FEATURE [Part::Extrusion] Extrude124
  Base = -> rect117948_1_5_1_8
  Dir = (0,0,1)
  DirMode = 0
  FaceMakerClass = Part::FaceMakerBullseye
  LengthFwd = 2
  LengthRev = 0
  Solid = true
  Symmetric = false
FEATURE [Part::Extrusion] Extrude125
  Base = -> rect117948_2_0_8_5_8
  Dir = (0,0,1)
  DirMode = 0
  FaceMakerClass = Part::FaceMakerBullseye
  LengthFwd = 2
  LengthRev = 0
  Solid = true
  Symmetric = false
FEATURE [Part::MultiFuse] Fusion001  label="wells_left"
  Placement = pos=(0,0,1) rot=(0,0,1;0rad)
  Shapes = -> [Extrude011,Extrude012,Extrude013,Extrude014,Extrude015,Extrude016,Extrude017,Extrude018,Extrude019,Extrude020,Extrude021,Extrude022,Extrude023,Extrude024,Extrude025,Extrude026,Extrude027,Extrude028,Extrude029,Extrude030,Extrude031,Extrude032,Extrude033,Extrude034,Extrude035,Extrude036,Extrude037,Extrude038,Extrude039,Extrude040,Extrude041,Extrude042,Extrude043,Extrude044,Extrude045,Extrude046,+79 more]
FEATURE [Part::Feature] path44149_5
  shape: bbox 139.5 x 94.73 x 2e-07 mm, 0 faces, 0 solids (baked)
FEATURE [Part::Extrusion] Extrude126  label="bounds_inner"
  Base = -> path44149_5
  Dir = (0,0,1)
  DirMode = 0
  FaceMakerClass = Part::FaceMakerBullseye
  LengthFwd = 1.6
  LengthRev = 0
  Placement = pos=(0,0,3) rot=(0,0,1;0rad)
  Solid = true
  Symmetric = false
FEATURE [Part::FeaturePython] XOR  label="bounds_full"  # WARN: FeaturePython — macro-defined, semantics opaque (R4)
  Objects = -> [Extrude,Fusion,Extrude126]
  Tolerance = 0
FEATURE [Part::FeaturePython] XOR001  label="bounds_left"  # WARN: FeaturePython — macro-defined, semantics opaque (R4)
  Objects = -> [Extrude,Fusion,Extrude126]
  Tolerance = 0
FEATURE [Part::FeaturePython] XOR002  label="bounds_full_copy"  # WARN: FeaturePython — macro-defined, semantics opaque (R4)
  Objects = -> [Extrude,Fusion,Extrude126]
  Tolerance = 0
FEATURE [Part::FeaturePython] XOR003  label="left"  # WARN: FeaturePython — macro-defined, semantics opaque (R4)
  Objects = -> [XOR001,Fusion001]
  Tolerance = 0
FEATURE [Part::Mirroring] Part__Mirroring  label="bounds_right"
  Base = (0,0,0)
  Normal = (1,0,0)
  Source = -> XOR002
FEATURE [Part::Feature] path52377_0_5_0_4_2_41_0_0_5_6_3
  shape: bbox 15 x 9.586 x 2e-07 mm, 0 faces, 0 solids (baked)
FEATURE [Part::Feature] path34096_2_0_9
  Placement = pos=(15.9497,-145.166,0) rot=(0,0,1;0rad)
  shape: bbox 2.208 x 2.415 x 2e-07 mm, 0 faces, 0 solids (baked)
FEATURE [Part::Feature] path34096_9_41
  Placement = pos=(20.9497,-147.266,0) rot=(0,0,1;0rad)
  shape: bbox 2.208 x 2.415 x 2e-07 mm, 0 faces, 0 solids (baked)
FEATURE [Part::Feature] path34072_1_9_4
  Placement = pos=(15.4497,-141.366,0) rot=(0,0,1;0rad)
  shape: bbox 1.877 x 2.052 x 2e-07 mm, 0 faces, 0 solids (baked)
FEATURE [Part::Feature] path34070_8_2
  Placement = pos=(20.9497,-141.366,0) rot=(0,0,1;0rad)
  shape: bbox 3.787 x 4.141 x 2e-07 mm, 0 faces, 0 solids (baked)
FEATURE [Part::Feature] path52377_0_5_0_4_2_41_0_0_5_6_5_4
  shape: bbox 15 x 9.586 x 2e-07 mm, 0 faces, 0 solids (baked)
FEATURE [Part::Feature] path34096_2_0_4_4
  Placement = pos=(15.9497,-145.166,0) rot=(0,0,1;0rad)
  shape: bbox 2.208 x 2.415 x 2e-07 mm, 0 faces, 0 solids (baked)
FEATURE [Part::Feature] path34096_9_4_6
  Placement = pos=(20.9497,-147.266,0) rot=(0,0,1;0rad)
  shape: bbox 2.208 x 2.415 x 2e-07 mm, 0 faces, 0 solids (baked)
FEATURE [Part::Feature] path34072_1_9_5_4
  Placement = pos=(15.4497,-141.366,0) rot=(0,0,1;0rad)
  shape: bbox 1.877 x 2.052 x 2e-07 mm, 0 faces, 0 solids (baked)
FEATURE [Part::Feature] path34070_8_0_7
  Placement = pos=(20.9497,-141.366,0) rot=(0,0,1;0rad)
  shape: bbox 3.787 x 4.141 x 2e-07 mm, 0 faces, 0 solids (baked)
FEATURE [Part::Feature] path52377_0_5_0_4_2_41_0_0_5_6_1_72
  shape: bbox 15 x 9.586 x 2e-07 mm, 0 faces, 0 solids (baked)
FEATURE [Part::Feature] path34096_2_0_0_1
  Placement = pos=(15.9497,-145.166,0) rot=(0,0,1;0rad)
  shape: bbox 2.208 x 2.415 x 2e-07 mm, 0 faces, 0 solids (baked)
FEATURE [Part::Feature] path34096_9_5_9
  Placement = pos=(20.9497,-147.266,0) rot=(0,0,1;0rad)
  shape: bbox 2.208 x 2.415 x 2e-07 mm, 0 faces, 0 solids (baked)
FEATURE [Part::Feature] path34072_1_9_51_7
  Placement = pos=(15.4497,-141.366,0) rot=(0,0,1;0rad)
  shape: bbox 1.877 x 2.052 x 2e-07 mm, 0 faces, 0 solids (baked)
FEATURE [Part::Feature] path34070_8_4_67
  Placement = pos=(20.9497,-141.366,0) rot=(0,0,1;0rad)
  shape: bbox 3.787 x 4.141 x 2e-07 mm, 0 faces, 0 solids (baked)
FEATURE [Part::Feature] path52377_0_5_0_4_2_41_0_0_5_6_1_6_8
  shape: bbox 15 x 9.586 x 2e-07 mm, 0 faces, 0 solids (baked)
FEATURE [Part::Feature] path34096_2_0_0_2_1
  Placement = pos=(15.9497,-145.166,0) rot=(0,0,1;0rad)
  shape: bbox 2.208 x 2.415 x 2e-07 mm, 0 faces, 0 solids (baked)
FEATURE [Part::Feature] path34096_9_5_7_2
  Placement = pos=(20.9497,-147.266,0) rot=(0,0,1;0rad)
  shape: bbox 2.208 x 2.415 x 2e-07 mm, 0 faces, 0 solids (baked)
FEATURE [Part::Feature] path34072_1_9_51_2_2
  Placement = pos=(15.4497,-141.366,0) rot=(0,0,1;0rad)
  shape: bbox 1.877 x 2.052 x 2e-07 mm, 0 faces, 0 solids (baked)
FEATURE [Part::Feature] path34070_8_4_6_5
  Placement = pos=(20.9497,-141.366,0) rot=(0,0,1;0rad)
  shape: bbox 3.787 x 4.141 x 2e-07 mm, 0 faces, 0 solids (baked)
FEATURE [Part::Feature] path52377_0_5_0_4_2_41_0_0_5_6_5_7_8
  shape: bbox 15 x 9.586 x 2e-07 mm, 0 faces, 0 solids (baked)
FEATURE [Part::Feature] path34096_2_0_4_8_2
  Placement = pos=(15.9497,-145.166,0) rot=(0,0,1;0rad)
  shape: bbox 2.208 x 2.415 x 2e-07 mm, 0 faces, 0 solids (baked)
FEATURE [Part::Feature] path34096_9_4_8_3
  Placement = pos=(20.9497,-147.266,0) rot=(0,0,1;0rad)
  shape: bbox 2.208 x 2.415 x 2e-07 mm, 0 faces, 0 solids (baked)
FEATURE [Part::Feature] path34072_1_9_5_5_3
  Placement = pos=(15.4497,-141.366,0) rot=(0,0,1;0rad)
  shape: bbox 1.877 x 2.052 x 2e-07 mm, 0 faces, 0 solids (baked)
FEATURE [Part::Feature] path34070_8_0_8_0
  Placement = pos=(20.9497,-141.366,0) rot=(0,0,1;0rad)
  shape: bbox 3.787 x 4.141 x 2e-07 mm, 0 faces, 0 solids (baked)
FEATURE [Part::Feature] path52377_0_5_0_4_2_41_0_0_5_6_1_7_3
  shape: bbox 15 x 9.586 x 2e-07 mm, 0 faces, 0 solids (baked)
FEATURE [Part::Feature] path34096_2_0_0_4_6
  Placement = pos=(15.9497,-145.166,0) rot=(0,0,1;0rad)
  shape: bbox 2.208 x 2.415 x 2e-07 mm, 0 faces, 0 solids (baked)
FEATURE [Part::Feature] path34096_9_5_75_6
  Placement = pos=(20.9497,-147.266,0) rot=(0,0,1;0rad)
  shape: bbox 2.208 x 2.415 x 2e-07 mm, 0 faces, 0 solids (baked)
FEATURE [Part::Feature] path34072_1_9_51_8_19
  Placement = pos=(15.4497,-141.366,0) rot=(0,0,1;0rad)
  shape: bbox 1.877 x 2.052 x 2e-07 mm, 0 faces, 0 solids (baked)
FEATURE [Part::Feature] path34070_8_4_65_4
  Placement = pos=(20.9497,-141.366,0) rot=(0,0,1;0rad)
  shape: bbox 3.787 x 4.141 x 2e-07 mm, 0 faces, 0 solids (baked)
FEATURE [Part::Feature] path52377_0_5_0_4_2_41_0_0_5_6_1_6_5_7
  shape: bbox 15 x 9.586 x 2e-07 mm, 0 faces, 0 solids (baked)
FEATURE [Part::Feature] path34096_2_0_0_2_7_8
  Placement = pos=(15.9497,-145.166,0) rot=(0,0,1;0rad)
  shape: bbox 2.208 x 2.415 x 2e-07 mm, 0 faces, 0 solids (baked)
FEATURE [Part::Feature] path34096_9_5_7_9_1
  Placement = pos=(20.9497,-147.266,0) rot=(0,0,1;0rad)
  shape: bbox 2.208 x 2.415 x 2e-07 mm, 0 faces, 0 solids (baked)
FEATURE [Part::Feature] path34072_1_9_51_2_1_34
  Placement = pos=(15.4497,-141.366,0) rot=(0,0,1;0rad)
  shape: bbox 1.877 x 2.052 x 2e-07 mm, 0 faces, 0 solids (baked)
FEATURE [Part::Feature] path34070_8_4_6_1_2
  Placement = pos=(20.9497,-141.366,0) rot=(0,0,1;0rad)
  shape: bbox 3.787 x 4.141 x 2e-07 mm, 0 faces, 0 solids (baked)
FEATURE [Part::Feature] path52377_0_5_0_4_2_41_0_0_5_6_5_7_1_8
  shape: bbox 15 x 9.586 x 2e-07 mm, 0 faces, 0 solids (baked)
FEATURE [Part::Feature] path34096_2_0_4_8_5_2
  Placement = pos=(15.9497,-145.166,0) rot=(0,0,1;0rad)
  shape: bbox 2.208 x 2.415 x 2e-07 mm, 0 faces, 0 solids (baked)
FEATURE [Part::Feature] path34096_9_4_8_5_7
  Placement = pos=(20.9497,-147.266,0) rot=(0,0,1;0rad)
  shape: bbox 2.208 x 2.415 x 2e-07 mm, 0 faces, 0 solids (baked)
FEATURE [Part::Feature] path34072_1_9_5_5_4_7
  Placement = pos=(15.4497,-141.366,0) rot=(0,0,1;0rad)
  shape: bbox 1.877 x 2.052 x 2e-07 mm, 0 faces, 0 solids (baked)
FEATURE [Part::Feature] path34070_8_0_8_3_5
  Placement = pos=(20.9497,-141.366,0) rot=(0,0,1;0rad)
  shape: bbox 3.787 x 4.141 x 2e-07 mm, 0 faces, 0 solids (baked)
FEATURE [Part::Feature] path52377_0_5_0_4_2_41_0_0_5_6_1_7_8_4
  shape: bbox 15 x 9.586 x 2e-07 mm, 0 faces, 0 solids (baked)
FEATURE [Part::Feature] path34096_2_0_0_4_5_1
  Placement = pos=(15.9497,-145.166,0) rot=(0,0,1;0rad)
  shape: bbox 2.208 x 2.415 x 2e-07 mm, 0 faces, 0 solids (baked)
FEATURE [Part::Feature] path34096_9_5_75_5_5
  Placement = pos=(20.9497,-147.266,0) rot=(0,0,1;0rad)
  shape: bbox 2.208 x 2.415 x 2e-07 mm, 0 faces, 0 solids (baked)
FEATURE [Part::Feature] path34072_1_9_51_8_1_9
  Placement = pos=(15.4497,-141.366,0) rot=(0,0,1;0rad)
  shape: bbox 1.877 x 2.052 x 2e-07 mm, 0 faces, 0 solids (baked)
FEATURE [Part::Feature] path34070_8_4_65_1_2
  Placement = pos=(20.9497,-141.366,0) rot=(0,0,1;0rad)
  shape: bbox 3.787 x 4.141 x 2e-07 mm, 0 faces, 0 solids (baked)
FEATURE [Part::Feature] path52377_0_5_0_4_2_41_0_0_5_6_1_6_5_2_8
  shape: bbox 15 x 9.586 x 2e-07 mm, 0 faces, 0 solids (baked)
FEATURE [Part::Feature] path34096_2_0_0_2_7_9_0
  Placement = pos=(15.9497,-145.166,0) rot=(0,0,1;0rad)
  shape: bbox 2.208 x 2.415 x 2e-07 mm, 0 faces, 0 solids (baked)
FEATURE [Part::Feature] path34096_9_5_7_9_4_5
  Placement = pos=(20.9497,-147.266,0) rot=(0,0,1;0rad)
  shape: bbox 2.208 x 2.415 x 2e-07 mm, 0 faces, 0 solids (baked)
FEATURE [Part::Feature] path34072_1_9_51_2_1_3_2
  Placement = pos=(15.4497,-141.366,0) rot=(0,0,1;0rad)
  shape: bbox 1.877 x 2.052 x 2e-07 mm, 0 faces, 0 solids (baked)
FEATURE [Part::Feature] path34070_8_4_6_1_4_3
  Placement = pos=(20.9497,-141.366,0) rot=(0,0,1;0rad)
  shape: bbox 3.787 x 4.141 x 2e-07 mm, 0 faces, 0 solids (baked)
FEATURE [Part::Feature] path52377_0_5_0_4_2_41_0_0_5_6_5_7_1_6_7
  shape: bbox 15 x 9.586 x 2e-07 mm, 0 faces, 0 solids (baked)
FEATURE [Part::Feature] path34096_2_0_4_8_5_4_5
  Placement = pos=(15.9497,-145.166,0) rot=(0,0,1;0rad)
  shape: bbox 2.208 x 2.415 x 2e-07 mm, 0 faces, 0 solids (baked)
FEATURE [Part::Feature] path34096_9_4_8_5_3_2
  Placement = pos=(20.9497,-147.266,0) rot=(0,0,1;0rad)
  shape: bbox 2.208 x 2.415 x 2e-07 mm, 0 faces, 0 solids (baked)
FEATURE [Part::Feature] path34072_1_9_5_5_4_4_8
  Placement = pos=(15.4497,-141.366,0) rot=(0,0,1;0rad)
  shape: bbox 1.877 x 2.052 x 2e-07 mm, 0 faces, 0 solids (baked)
FEATURE [Part::Feature] path34070_8_0_8_3_3_6
  Placement = pos=(20.9497,-141.366,0) rot=(0,0,1;0rad)
  shape: bbox 3.787 x 4.141 x 2e-07 mm, 0 faces, 0 solids (baked)
FEATURE [Part::Feature] path52377_0_5_0_4_2_41_0_0_5_6_1_7_9_1
  shape: bbox 15 x 9.586 x 2e-07 mm, 0 faces, 0 solids (baked)
FEATURE [Part::Feature] path34096_2_0_0_4_52_2
  Placement = pos=(15.9497,-145.166,0) rot=(0,0,1;0rad)
  shape: bbox 2.208 x 2.415 x 2e-07 mm, 0 faces, 0 solids (baked)
FEATURE [Part::Feature] path34096_9_5_75_2_7
  Placement = pos=(20.9497,-147.266,0) rot=(0,0,1;0rad)
  shape: bbox 2.208 x 2.415 x 2e-07 mm, 0 faces, 0 solids (baked)
FEATURE [Part::Feature] path34072_1_9_51_8_2_4
  Placement = pos=(15.4497,-141.366,0) rot=(0,0,1;0rad)
  shape: bbox 1.877 x 2.052 x 2e-07 mm, 0 faces, 0 solids (baked)
FEATURE [Part::Feature] path34070_8_4_65_5_8
  Placement = pos=(20.9497,-141.366,0) rot=(0,0,1;0rad)
  shape: bbox 3.787 x 4.141 x 2e-07 mm, 0 faces, 0 solids (baked)
FEATURE [Part::Feature] path52377_0_5_0_4_2_41_0_0_5_6_1_6_5_3_5
  shape: bbox 15 x 9.586 x 2e-07 mm, 0 faces, 0 solids (baked)
FEATURE [Part::Feature] path34096_2_0_0_2_7_3_1
  Placement = pos=(15.9497,-145.166,0) rot=(0,0,1;0rad)
  shape: bbox 2.208 x 2.415 x 2e-07 mm, 0 faces, 0 solids (baked)
FEATURE [Part::Feature] path34096_9_5_7_9_0_9
  Placement = pos=(20.9497,-147.266,0) rot=(0,0,1;0rad)
  shape: bbox 2.208 x 2.415 x 2e-07 mm, 0 faces, 0 solids (baked)
FEATURE [Part::Feature] path34072_1_9_51_2_1_9_3
  Placement = pos=(15.4497,-141.366,0) rot=(0,0,1;0rad)
  shape: bbox 1.877 x 2.052 x 2e-07 mm, 0 faces, 0 solids (baked)
FEATURE [Part::Feature] path34070_8_4_6_1_5_3
  Placement = pos=(20.9497,-141.366,0) rot=(0,0,1;0rad)
  shape: bbox 3.787 x 4.141 x 2e-07 mm, 0 faces, 0 solids (baked)
FEATURE [Part::Feature] path52377_0_5_0_4_2_41_0_0_5_6_5_7_1_9_1
  shape: bbox 15 x 9.586 x 2e-07 mm, 0 faces, 0 solids (baked)
FEATURE [Part::Feature] path34096_2_0_4_8_5_1_8
  Placement = pos=(15.9497,-145.166,0) rot=(0,0,1;0rad)
  shape: bbox 2.208 x 2.415 x 2e-07 mm, 0 faces, 0 solids (baked)
FEATURE [Part::Feature] path34096_9_4_8_5_9_93
  Placement = pos=(20.9497,-147.266,0) rot=(0,0,1;0rad)
  shape: bbox 2.208 x 2.415 x 2e-07 mm, 0 faces, 0 solids (baked)
FEATURE [Part::Feature] path34072_1_9_5_5_4_3_8
  Placement = pos=(15.4497,-141.366,0) rot=(0,0,1;0rad)
  shape: bbox 1.877 x 2.052 x 2e-07 mm, 0 faces, 0 solids (baked)
FEATURE [Part::Feature] path34070_8_0_8_3_8_7
  Placement = pos=(20.9497,-141.366,0) rot=(0,0,1;0rad)
  shape: bbox 3.787 x 4.141 x 2e-07 mm, 0 faces, 0 solids (baked)
FEATURE [Part::Feature] path52377_0_5_0_4_2_41_0_0_5_6_1_7_0_4
  shape: bbox 15 x 9.586 x 2e-07 mm, 0 faces, 0 solids (baked)
FEATURE [Part::Feature] path34096_2_0_0_4_9_0
  Placement = pos=(15.9497,-145.166,0) rot=(0,0,1;0rad)
  shape: bbox 2.208 x 2.415 x 2e-07 mm, 0 faces, 0 solids (baked)
FEATURE [Part::Feature] path34096_9_5_75_3_1
  Placement = pos=(20.9497,-147.266,0) rot=(0,0,1;0rad)
  shape: bbox 2.208 x 2.415 x 2e-07 mm, 0 faces, 0 solids (baked)
FEATURE [Part::Feature] path34072_1_9_51_8_3_7
  Placement = pos=(15.4497,-141.366,0) rot=(0,0,1;0rad)
  shape: bbox 1.877 x 2.052 x 2e-07 mm, 0 faces, 0 solids (baked)
FEATURE [Part::Feature] path34070_8_4_65_6_0
  Placement = pos=(20.9497,-141.366,0) rot=(0,0,1;0rad)
  shape: bbox 3.787 x 4.141 x 2e-07 mm, 0 faces, 0 solids (baked)
FEATURE [Part::Feature] path52377_0_5_0_4_2_41_0_0_5_6_1_6_5_0_5
  shape: bbox 15 x 9.586 x 2e-07 mm, 0 faces, 0 solids (baked)
FEATURE [Part::Feature] path34096_2_0_0_2_7_5_5
  Placement = pos=(15.9497,-145.166,0) rot=(0,0,1;0rad)
  shape: bbox 2.208 x 2.415 x 2e-07 mm, 0 faces, 0 solids (baked)
FEATURE [Part::Feature] path34096_9_5_7_9_2_7
  Placement = pos=(20.9497,-147.266,0) rot=(0,0,1;0rad)
  shape: bbox 2.208 x 2.415 x 2e-07 mm, 0 faces, 0 solids (baked)
FEATURE [Part::Feature] path34072_1_9_51_2_1_4_4
  Placement = pos=(15.4497,-141.366,0) rot=(0,0,1;0rad)
  shape: bbox 1.877 x 2.052 x 2e-07 mm, 0 faces, 0 solids (baked)
FEATURE [Part::Feature] path34070_8_4_6_1_1_1
  Placement = pos=(20.9497,-141.366,0) rot=(0,0,1;0rad)
  shape: bbox 3.787 x 4.141 x 2e-07 mm, 0 faces, 0 solids (baked)
FEATURE [Part::Feature] path52377_0_5_0_4_2_41_0_0_5_6_5_7_1_3_9
  shape: bbox 15 x 9.586 x 2e-07 mm, 0 faces, 0 solids (baked)
FEATURE [Part::Feature] path34096_2_0_4_8_5_3_9
  Placement = pos=(15.9497,-145.166,0) rot=(0,0,1;0rad)
  shape: bbox 2.208 x 2.415 x 2e-07 mm, 0 faces, 0 solids (baked)
FEATURE [Part::Feature] path34096_9_4_8_5_8_7
  Placement = pos=(20.9497,-147.266,0) rot=(0,0,1;0rad)
  shape: bbox 2.208 x 2.415 x 2e-07 mm, 0 faces, 0 solids (baked)
FEATURE [Part::Feature] path34072_1_9_5_5_4_31_0
  Placement = pos=(15.4497,-141.366,0) rot=(0,0,1;0rad)
  shape: bbox 1.877 x 2.052 x 2e-07 mm, 0 faces, 0 solids (baked)
FEATURE [Part::Feature] path34070_8_0_8_3_1_3
  Placement = pos=(20.9497,-141.366,0) rot=(0,0,1;0rad)
  shape: bbox 3.787 x 4.141 x 2e-07 mm, 0 faces, 0 solids (baked)
FEATURE [Part::Feature] path52377_0_5_0_4_2_41_0_0_5_6_5_7_1_9_7_7
  shape: bbox 15.59 x 9.627 x 2e-07 mm, 0 faces, 0 solids (baked)
FEATURE [Part::Feature] path34096_2_0_4_8_5_1_5_05
  Placement = pos=(15.9497,-145.166,0) rot=(0,0,1;0rad)
  shape: bbox 2.407 x 2.351 x 2e-07 mm, 0 faces, 0 solids (baked)
FEATURE [Part::Feature] path34096_9_4_8_5_9_9_09
  Placement = pos=(20.9497,-147.266,0) rot=(0,0,1;0rad)
  shape: bbox 2.407 x 2.351 x 2e-07 mm, 0 faces, 0 solids (baked)
FEATURE [Part::Feature] path34072_1_9_5_5_4_3_4_3
  Placement = pos=(15.4497,-141.366,0) rot=(0,0,1;0rad)
  shape: bbox 2.046 x 1.999 x 2e-07 mm, 0 faces, 0 solids (baked)
FEATURE [Part::Feature] path34070_8_0_8_3_8_5_5
  Placement = pos=(20.9497,-141.366,0) rot=(0,0,1;0rad)
  shape: bbox 4.128 x 4.033 x 2e-07 mm, 0 faces, 0 solids (baked)
FEATURE [Part::Feature] path52377_0_5_0_4_2_41_0_0_5_6_5_7_1_9_7_1_8
  shape: bbox 16.06 x 7.96 x 2e-07 mm, 0 faces, 0 solids (baked)
FEATURE [Part::Feature] path34096_2_0_4_8_5_1_5_0_30
  Placement = pos=(15.9497,-145.166,0) rot=(0,0,1;0rad)
  shape: bbox 2.384 x 2.386 x 2e-07 mm, 0 faces, 0 solids (baked)
FEATURE [Part::Feature] path34096_9_4_8_5_9_9_0_41
  Placement = pos=(20.9497,-147.266,0) rot=(0,0,1;0rad)
  shape: bbox 2.384 x 2.386 x 2e-07 mm, 0 faces, 0 solids (baked)
FEATURE [Part::Feature] path34072_1_9_5_5_4_3_4_2_7
  Placement = pos=(15.4497,-141.366,0) rot=(0,0,1;0rad)
  shape: bbox 2.027 x 2.028 x 2e-07 mm, 0 faces, 0 solids (baked)
FEATURE [Part::Feature] path34070_8_0_8_3_8_5_0_9
  Placement = pos=(20.9497,-141.366,0) rot=(0,0,1;0rad)
  shape: bbox 4.089 x 4.091 x 2e-07 mm, 0 faces, 0 solids (baked)
FEATURE [Part::Feature] path52377_0_5_0_4_2_41_0_0_5_6_5_7_1_9_7_1_9_3
  shape: bbox 15.44 x 9.291 x 2e-07 mm, 0 faces, 0 solids (baked)
FEATURE [Part::Feature] path34096_2_0_4_8_5_1_5_0_3_2
  Placement = pos=(15.9497,-145.166,0) rot=(0,0,1;0rad)
  shape: bbox 2.351 x 2.407 x 2e-07 mm, 0 faces, 0 solids (baked)
FEATURE [Part::Feature] path34096_9_4_8_5_9_9_0_4_9
  Placement = pos=(20.9497,-147.266,0) rot=(0,0,1;0rad)
  shape: bbox 2.351 x 2.407 x 2e-07 mm, 0 faces, 0 solids (baked)
FEATURE [Part::Feature] path34072_1_9_5_5_4_3_4_2_6_9
  Placement = pos=(15.4497,-141.366,0) rot=(0,0,1;0rad)
  shape: bbox 1.999 x 2.046 x 2e-07 mm, 0 faces, 0 solids (baked)
FEATURE [Part::Feature] path34070_8_0_8_3_8_5_0_4_8
  Placement = pos=(20.9497,-141.366,0) rot=(0,0,1;0rad)
  shape: bbox 4.033 x 4.128 x 2e-07 mm, 0 faces, 0 solids (baked)
FEATURE [Part::Feature] path52377_0_5_0_4_2_41_0_0_5_6_5_7_1_9_7_1_1_8
  shape: bbox 14.99 x 10.79 x 2e-07 mm, 0 faces, 0 solids (baked)
FEATURE [Part::Feature] path34096_2_0_4_8_5_1_5_0_5_9
  Placement = pos=(15.9497,-145.166,0) rot=(0,0,1;0rad)
  shape: bbox 2.386 x 2.384 x 2e-07 mm, 0 faces, 0 solids (baked)
FEATURE [Part::Feature] path34096_9_4_8_5_9_9_0_8_7
  Placement = pos=(20.9497,-147.266,0) rot=(0,0,1;0rad)
  shape: bbox 2.386 x 2.384 x 2e-07 mm, 0 faces, 0 solids (baked)
FEATURE [Part::Feature] path34072_1_9_5_5_4_3_4_2_3_0
  Placement = pos=(15.4497,-141.366,0) rot=(0,0,1;0rad)
  shape: bbox 2.028 x 2.027 x 2e-07 mm, 0 faces, 0 solids (baked)
FEATURE [Part::Feature] path34070_8_0_8_3_8_5_0_7_8
  Placement = pos=(20.9497,-141.366,0) rot=(0,0,1;0rad)
  shape: bbox 4.091 x 4.089 x 2e-07 mm, 0 faces, 0 solids (baked)
FEATURE [Part::Feature] path37937_8_6
  shape: bbox 1.702 x 2 x 2e-07 mm, 0 faces, 0 solids (baked)
FEATURE [Part::Feature] path37931_6_7
  shape: bbox 1.7 x 2 x 2e-07 mm, 0 faces, 0 solids (baked)
FEATURE [Part::Feature] path37321_9_5
  shape: bbox 2.002 x 1.603 x 2e-07 mm, 0 faces, 0 solids (baked)
FEATURE [Part::Feature] path37327_3_6
  shape: bbox 2.002 x 1.601 x 2e-07 mm, 0 faces, 0 solids (baked)
FEATURE [Part::Feature] path37329_6_1
  shape: bbox 2.002 x 1.603 x 2e-07 mm, 0 faces, 0 solids (baked)
FEATURE [Part::Feature] path37333_00_0
  shape: bbox 2.002 x 1.603 x 2e-07 mm, 0 faces, 0 solids (baked)
FEATURE [Part::Feature] circle37301_1_8
  Placement = pos=(131.24,-64.4621,0) rot=(0,0,1;0rad)
  shape: bbox 0.8832 x 0.9658 x 2e-07 mm, 0 faces, 0 solids (baked)
FEATURE [Part::Feature] circle37295_7_4
  Placement = pos=(138.24,-64.4621,0) rot=(0,0,1;0rad)
  shape: bbox 0.8832 x 0.9658 x 2e-07 mm, 0 faces, 0 solids (baked)
FEATURE [Part::Feature] rect117948_11_2
  shape: bbox 1.7 x 49.96 x 2e-07 mm, 0 faces, 0 solids (baked)
FEATURE [Part::Feature] rect117948_2_00_4
  shape: bbox 1.7 x 49.96 x 2e-07 mm, 0 faces, 0 solids (baked)
FEATURE [Part::Extrusion] Extrude127
  Base = -> path52377_0_5_0_4_2_41_0_0_5_6_3
  Dir = (0,0,1)
  DirMode = 0
  FaceMakerClass = Part::FaceMakerBullseye
  LengthFwd = 2
  LengthRev = 0
  Solid = true
  Symmetric = false
FEATURE [Part::Extrusion] Extrude128
  Base = -> path34096_2_0_9
  Dir = (0,0,1)
  DirMode = 0
  FaceMakerClass = Part::FaceMakerBullseye
  LengthFwd = 2
  LengthRev = 0
  Solid = true
  Symmetric = false
FEATURE [Part::Extrusion] Extrude129
  Base = -> path34096_9_41
  Dir = (0,0,1)
  DirMode = 0
  FaceMakerClass = Part::FaceMakerBullseye
  LengthFwd = 2
  LengthRev = 0
  Solid = true
  Symmetric = false
FEATURE [Part::Extrusion] Extrude130
  Base = -> path34072_1_9_4
  Dir = (0,0,1)
  DirMode = 0
  FaceMakerClass = Part::FaceMakerBullseye
  LengthFwd = 2
  LengthRev = 0
  Solid = true
  Symmetric = false
FEATURE [Part::Extrusion] Extrude131
  Base = -> path34070_8_2
  Dir = (0,0,1)
  DirMode = 0
  FaceMakerClass = Part::FaceMakerBullseye
  LengthFwd = 2
  LengthRev = 0
  Solid = true
  Symmetric = false
FEATURE [Part::Extrusion] Extrude132
  Base = -> path52377_0_5_0_4_2_41_0_0_5_6_5_4
  Dir = (0,0,1)
  DirMode = 0
  FaceMakerClass = Part::FaceMakerBullseye
  LengthFwd = 2
  LengthRev = 0
  Solid = true
  Symmetric = false
FEATURE [Part::Extrusion] Extrude133
  Base = -> path34096_2_0_4_4
  Dir = (0,0,1)
  DirMode = 0
  FaceMakerClass = Part::FaceMakerBullseye
  LengthFwd = 2
  LengthRev = 0
  Solid = true
  Symmetric = false
FEATURE [Part::Extrusion] Extrude134
  Base = -> path34096_9_4_6
  Dir = (0,0,1)
  DirMode = 0
  FaceMakerClass = Part::FaceMakerBullseye
  LengthFwd = 2
  LengthRev = 0
  Solid = true
  Symmetric = false
FEATURE [Part::Extrusion] Extrude135
  Base = -> path34072_1_9_5_4
  Dir = (0,0,1)
  DirMode = 0
  FaceMakerClass = Part::FaceMakerBullseye
  LengthFwd = 2
  LengthRev = 0
  Solid = true
  Symmetric = false
FEATURE [Part::Extrusion] Extrude136
  Base = -> path34070_8_0_7
  Dir = (0,0,1)
  DirMode = 0
  FaceMakerClass = Part::FaceMakerBullseye
  LengthFwd = 2
  LengthRev = 0
  Solid = true
  Symmetric = false
FEATURE [Part::Extrusion] Extrude137
  Base = -> path52377_0_5_0_4_2_41_0_0_5_6_1_72
  Dir = (0,0,1)
  DirMode = 0
  FaceMakerClass = Part::FaceMakerBullseye
  LengthFwd = 2
  LengthRev = 0
  Solid = true
  Symmetric = false
FEATURE [Part::Extrusion] Extrude138
  Base = -> path34096_2_0_0_1
  Dir = (0,0,1)
  DirMode = 0
  FaceMakerClass = Part::FaceMakerBullseye
  LengthFwd = 2
  LengthRev = 0
  Solid = true
  Symmetric = false
FEATURE [Part::Extrusion] Extrude139
  Base = -> path34096_9_5_9
  Dir = (0,0,1)
  DirMode = 0
  FaceMakerClass = Part::FaceMakerBullseye
  LengthFwd = 2
  LengthRev = 0
  Solid = true
  Symmetric = false
FEATURE [Part::Extrusion] Extrude140
  Base = -> path34072_1_9_51_7
  Dir = (0,0,1)
  DirMode = 0
  FaceMakerClass = Part::FaceMakerBullseye
  LengthFwd = 2
  LengthRev = 0
  Solid = true
  Symmetric = false
FEATURE [Part::Extrusion] Extrude141
  Base = -> path34070_8_4_67
  Dir = (0,0,1)
  DirMode = 0
  FaceMakerClass = Part::FaceMakerBullseye
  LengthFwd = 2
  LengthRev = 0
  Solid = true
  Symmetric = false
FEATURE [Part::Extrusion] Extrude142
  Base = -> path52377_0_5_0_4_2_41_0_0_5_6_1_6_8
  Dir = (0,0,1)
  DirMode = 0
  FaceMakerClass = Part::FaceMakerBullseye
  LengthFwd = 2
  LengthRev = 0
  Solid = true
  Symmetric = false
FEATURE [Part::Extrusion] Extrude143
  Base = -> path34096_2_0_0_2_1
  Dir = (0,0,1)
  DirMode = 0
  FaceMakerClass = Part::FaceMakerBullseye
  LengthFwd = 2
  LengthRev = 0
  Solid = true
  Symmetric = false
FEATURE [Part::Extrusion] Extrude144
  Base = -> path34096_9_5_7_2
  Dir = (0,0,1)
  DirMode = 0
  FaceMakerClass = Part::FaceMakerBullseye
  LengthFwd = 2
  LengthRev = 0
  Solid = true
  Symmetric = false
FEATURE [Part::Extrusion] Extrude145
  Base = -> path34072_1_9_51_2_2
  Dir = (0,0,1)
  DirMode = 0
  FaceMakerClass = Part::FaceMakerBullseye
  LengthFwd = 2
  LengthRev = 0
  Solid = true
  Symmetric = false
FEATURE [Part::Extrusion] Extrude146
  Base = -> path34070_8_4_6_5
  Dir = (0,0,1)
  DirMode = 0
  FaceMakerClass = Part::FaceMakerBullseye
  LengthFwd = 2
  LengthRev = 0
  Solid = true
  Symmetric = false
FEATURE [Part::Extrusion] Extrude147
  Base = -> path52377_0_5_0_4_2_41_0_0_5_6_5_7_8
  Dir = (0,0,1)
  DirMode = 0
  FaceMakerClass = Part::FaceMakerBullseye
  LengthFwd = 2
  LengthRev = 0
  Solid = true
  Symmetric = false
FEATURE [Part::Extrusion] Extrude148
  Base = -> path34096_2_0_4_8_2
  Dir = (0,0,1)
  DirMode = 0
  FaceMakerClass = Part::FaceMakerBullseye
  LengthFwd = 2
  LengthRev = 0
  Solid = true
  Symmetric = false
FEATURE [Part::Extrusion] Extrude149
  Base = -> path34096_9_4_8_3
  Dir = (0,0,1)
  DirMode = 0
  FaceMakerClass = Part::FaceMakerBullseye
  LengthFwd = 2
  LengthRev = 0
  Solid = true
  Symmetric = false
FEATURE [Part::Extrusion] Extrude150
  Base = -> path34072_1_9_5_5_3
  Dir = (0,0,1)
  DirMode = 0
  FaceMakerClass = Part::FaceMakerBullseye
  LengthFwd = 2
  LengthRev = 0
  Solid = true
  Symmetric = false
FEATURE [Part::Extrusion] Extrude151
  Base = -> path34070_8_0_8_0
  Dir = (0,0,1)
  DirMode = 0
  FaceMakerClass = Part::FaceMakerBullseye
  LengthFwd = 2
  LengthRev = 0
  Solid = true
  Symmetric = false
FEATURE [Part::Extrusion] Extrude152
  Base = -> path52377_0_5_0_4_2_41_0_0_5_6_1_7_3
  Dir = (0,0,1)
  DirMode = 0
  FaceMakerClass = Part::FaceMakerBullseye
  LengthFwd = 2
  LengthRev = 0
  Solid = true
  Symmetric = false
FEATURE [Part::Extrusion] Extrude153
  Base = -> path34096_2_0_0_4_6
  Dir = (0,0,1)
  DirMode = 0
  FaceMakerClass = Part::FaceMakerBullseye
  LengthFwd = 2
  LengthRev = 0
  Solid = true
  Symmetric = false
FEATURE [Part::Extrusion] Extrude154
  Base = -> path34096_9_5_75_6
  Dir = (0,0,1)
  DirMode = 0
  FaceMakerClass = Part::FaceMakerBullseye
  LengthFwd = 2
  LengthRev = 0
  Solid = true
  Symmetric = false
FEATURE [Part::Extrusion] Extrude155
  Base = -> path34072_1_9_51_8_19
  Dir = (0,0,1)
  DirMode = 0
  FaceMakerClass = Part::FaceMakerBullseye
  LengthFwd = 2
  LengthRev = 0
  Solid = true
  Symmetric = false
FEATURE [Part::Extrusion] Extrude156
  Base = -> path34070_8_4_65_4
  Dir = (0,0,1)
  DirMode = 0
  FaceMakerClass = Part::FaceMakerBullseye
  LengthFwd = 2
  LengthRev = 0
  Solid = true
  Symmetric = false
FEATURE [Part::Extrusion] Extrude157
  Base = -> path52377_0_5_0_4_2_41_0_0_5_6_1_6_5_7
  Dir = (0,0,1)
  DirMode = 0
  FaceMakerClass = Part::FaceMakerBullseye
  LengthFwd = 2
  LengthRev = 0
  Solid = true
  Symmetric = false
FEATURE [Part::Extrusion] Extrude158
  Base = -> path34096_2_0_0_2_7_8
  Dir = (0,0,1)
  DirMode = 0
  FaceMakerClass = Part::FaceMakerBullseye
  LengthFwd = 2
  LengthRev = 0
  Solid = true
  Symmetric = false
FEATURE [Part::Extrusion] Extrude159
  Base = -> path34096_9_5_7_9_1
  Dir = (0,0,1)
  DirMode = 0
  FaceMakerClass = Part::FaceMakerBullseye
  LengthFwd = 2
  LengthRev = 0
  Solid = true
  Symmetric = false
FEATURE [Part::Extrusion] Extrude160
  Base = -> path34072_1_9_51_2_1_34
  Dir = (0,0,1)
  DirMode = 0
  FaceMakerClass = Part::FaceMakerBullseye
  LengthFwd = 2
  LengthRev = 0
  Solid = true
  Symmetric = false
FEATURE [Part::Extrusion] Extrude161
  Base = -> path34070_8_4_6_1_2
  Dir = (0,0,1)
  DirMode = 0
  FaceMakerClass = Part::FaceMakerBullseye
  LengthFwd = 2
  LengthRev = 0
  Solid = true
  Symmetric = false
FEATURE [Part::Extrusion] Extrude162
  Base = -> path52377_0_5_0_4_2_41_0_0_5_6_5_7_1_8
  Dir = (0,0,1)
  DirMode = 0
  FaceMakerClass = Part::FaceMakerBullseye
  LengthFwd = 2
  LengthRev = 0
  Solid = true
  Symmetric = false
FEATURE [Part::Extrusion] Extrude163
  Base = -> path34096_2_0_4_8_5_2
  Dir = (0,0,1)
  DirMode = 0
  FaceMakerClass = Part::FaceMakerBullseye
  LengthFwd = 2
  LengthRev = 0
  Solid = true
  Symmetric = false
FEATURE [Part::Extrusion] Extrude164
  Base = -> path34096_9_4_8_5_7
  Dir = (0,0,1)
  DirMode = 0
  FaceMakerClass = Part::FaceMakerBullseye
  LengthFwd = 2
  LengthRev = 0
  Solid = true
  Symmetric = false
FEATURE [Part::Extrusion] Extrude165
  Base = -> path34072_1_9_5_5_4_7
  Dir = (0,0,1)
  DirMode = 0
  FaceMakerClass = Part::FaceMakerBullseye
  LengthFwd = 2
  LengthRev = 0
  Solid = true
  Symmetric = false
FEATURE [Part::Extrusion] Extrude166
  Base = -> path34070_8_0_8_3_5
  Dir = (0,0,1)
  DirMode = 0
  FaceMakerClass = Part::FaceMakerBullseye
  LengthFwd = 2
  LengthRev = 0
  Solid = true
  Symmetric = false
FEATURE [Part::Extrusion] Extrude167
  Base = -> path52377_0_5_0_4_2_41_0_0_5_6_1_7_8_4
  Dir = (0,0,1)
  DirMode = 0
  FaceMakerClass = Part::FaceMakerBullseye
  LengthFwd = 2
  LengthRev = 0
  Solid = true
  Symmetric = false
FEATURE [Part::Extrusion] Extrude168
  Base = -> path34096_2_0_0_4_5_1
  Dir = (0,0,1)
  DirMode = 0
  FaceMakerClass = Part::FaceMakerBullseye
  LengthFwd = 2
  LengthRev = 0
  Solid = true
  Symmetric = false
FEATURE [Part::Extrusion] Extrude169
  Base = -> path34096_9_5_75_5_5
  Dir = (0,0,1)
  DirMode = 0
  FaceMakerClass = Part::FaceMakerBullseye
  LengthFwd = 2
  LengthRev = 0
  Solid = true
  Symmetric = false
FEATURE [Part::Extrusion] Extrude170
  Base = -> path34072_1_9_51_8_1_9
  Dir = (0,0,1)
  DirMode = 0
  FaceMakerClass = Part::FaceMakerBullseye
  LengthFwd = 2
  LengthRev = 0
  Solid = true
  Symmetric = false
FEATURE [Part::Extrusion] Extrude171
  Base = -> path34070_8_4_65_1_2
  Dir = (0,0,1)
  DirMode = 0
  FaceMakerClass = Part::FaceMakerBullseye
  LengthFwd = 2
  LengthRev = 0
  Solid = true
  Symmetric = false
FEATURE [Part::Extrusion] Extrude172
  Base = -> path52377_0_5_0_4_2_41_0_0_5_6_1_6_5_2_8
  Dir = (0,0,1)
  DirMode = 0
  FaceMakerClass = Part::FaceMakerBullseye
  LengthFwd = 2
  LengthRev = 0
  Solid = true
  Symmetric = false
FEATURE [Part::Extrusion] Extrude173
  Base = -> path34096_2_0_0_2_7_9_0
  Dir = (0,0,1)
  DirMode = 0
  FaceMakerClass = Part::FaceMakerBullseye
  LengthFwd = 2
  LengthRev = 0
  Solid = true
  Symmetric = false
FEATURE [Part::Extrusion] Extrude174
  Base = -> path34096_9_5_7_9_4_5
  Dir = (0,0,1)
  DirMode = 0
  FaceMakerClass = Part::FaceMakerBullseye
  LengthFwd = 2
  LengthRev = 0
  Solid = true
  Symmetric = false
FEATURE [Part::Extrusion] Extrude175
  Base = -> path34072_1_9_51_2_1_3_2
  Dir = (0,0,1)
  DirMode = 0
  FaceMakerClass = Part::FaceMakerBullseye
  LengthFwd = 2
  LengthRev = 0
  Solid = true
  Symmetric = false
FEATURE [Part::Extrusion] Extrude176
  Base = -> path34070_8_4_6_1_4_3
  Dir = (0,0,1)
  DirMode = 0
  FaceMakerClass = Part::FaceMakerBullseye
  LengthFwd = 2
  LengthRev = 0
  Solid = true
  Symmetric = false
FEATURE [Part::Extrusion] Extrude177
  Base = -> path52377_0_5_0_4_2_41_0_0_5_6_5_7_1_6_7
  Dir = (0,0,1)
  DirMode = 0
  FaceMakerClass = Part::FaceMakerBullseye
  LengthFwd = 2
  LengthRev = 0
  Solid = true
  Symmetric = false
FEATURE [Part::Extrusion] Extrude178
  Base = -> path34096_2_0_4_8_5_4_5
  Dir = (0,0,1)
  DirMode = 0
  FaceMakerClass = Part::FaceMakerBullseye
  LengthFwd = 2
  LengthRev = 0
  Solid = true
  Symmetric = false
FEATURE [Part::Extrusion] Extrude179
  Base = -> path34096_9_4_8_5_3_2
  Dir = (0,0,1)
  DirMode = 0
  FaceMakerClass = Part::FaceMakerBullseye
  LengthFwd = 2
  LengthRev = 0
  Solid = true
  Symmetric = false
FEATURE [Part::Extrusion] Extrude180
  Base = -> path34072_1_9_5_5_4_4_8
  Dir = (0,0,1)
  DirMode = 0
  FaceMakerClass = Part::FaceMakerBullseye
  LengthFwd = 2
  LengthRev = 0
  Solid = true
  Symmetric = false
FEATURE [Part::Extrusion] Extrude181
  Base = -> path34070_8_0_8_3_3_6
  Dir = (0,0,1)
  DirMode = 0
  FaceMakerClass = Part::FaceMakerBullseye
  LengthFwd = 2
  LengthRev = 0
  Solid = true
  Symmetric = false
FEATURE [Part::Extrusion] Extrude182
  Base = -> path52377_0_5_0_4_2_41_0_0_5_6_1_7_9_1
  Dir = (0,0,1)
  DirMode = 0
  FaceMakerClass = Part::FaceMakerBullseye
  LengthFwd = 2
  LengthRev = 0
  Solid = true
  Symmetric = false
FEATURE [Part::Extrusion] Extrude183
  Base = -> path34096_2_0_0_4_52_2
  Dir = (0,0,1)
  DirMode = 0
  FaceMakerClass = Part::FaceMakerBullseye
  LengthFwd = 2
  LengthRev = 0
  Solid = true
  Symmetric = false
FEATURE [Part::Extrusion] Extrude184
  Base = -> path34096_9_5_75_2_7
  Dir = (0,0,1)
  DirMode = 0
  FaceMakerClass = Part::FaceMakerBullseye
  LengthFwd = 2
  LengthRev = 0
  Solid = true
  Symmetric = false
FEATURE [Part::Extrusion] Extrude185
  Base = -> path34072_1_9_51_8_2_4
  Dir = (0,0,1)
  DirMode = 0
  FaceMakerClass = Part::FaceMakerBullseye
  LengthFwd = 2
  LengthRev = 0
  Solid = true
  Symmetric = false
FEATURE [Part::Extrusion] Extrude186
  Base = -> path34070_8_4_65_5_8
  Dir = (0,0,1)
  DirMode = 0
  FaceMakerClass = Part::FaceMakerBullseye
  LengthFwd = 2
  LengthRev = 0
  Solid = true
  Symmetric = false
FEATURE [Part::Extrusion] Extrude187
  Base = -> path52377_0_5_0_4_2_41_0_0_5_6_1_6_5_3_5
  Dir = (0,0,1)
  DirMode = 0
  FaceMakerClass = Part::FaceMakerBullseye
  LengthFwd = 2
  LengthRev = 0
  Solid = true
  Symmetric = false
FEATURE [Part::Extrusion] Extrude188
  Base = -> path34096_2_0_0_2_7_3_1
  Dir = (0,0,1)
  DirMode = 0
  FaceMakerClass = Part::FaceMakerBullseye
  LengthFwd = 2
  LengthRev = 0
  Solid = true
  Symmetric = false
FEATURE [Part::Extrusion] Extrude189
  Base = -> path34096_9_5_7_9_0_9
  Dir = (0,0,1)
  DirMode = 0
  FaceMakerClass = Part::FaceMakerBullseye
  LengthFwd = 2
  LengthRev = 0
  Solid = true
  Symmetric = false
FEATURE [Part::Extrusion] Extrude190
  Base = -> path34072_1_9_51_2_1_9_3
  Dir = (0,0,1)
  DirMode = 0
  FaceMakerClass = Part::FaceMakerBullseye
  LengthFwd = 2
  LengthRev = 0
  Solid = true
  Symmetric = false
FEATURE [Part::Extrusion] Extrude191
  Base = -> path34070_8_4_6_1_5_3
  Dir = (0,0,1)
  DirMode = 0
  FaceMakerClass = Part::FaceMakerBullseye
  LengthFwd = 2
  LengthRev = 0
  Solid = true
  Symmetric = false
FEATURE [Part::Extrusion] Extrude192
  Base = -> path52377_0_5_0_4_2_41_0_0_5_6_5_7_1_9_1
  Dir = (0,0,1)
  DirMode = 0
  FaceMakerClass = Part::FaceMakerBullseye
  LengthFwd = 2
  LengthRev = 0
  Solid = true
  Symmetric = false
FEATURE [Part::Extrusion] Extrude193
  Base = -> path34096_2_0_4_8_5_1_8
  Dir = (0,0,1)
  DirMode = 0
  FaceMakerClass = Part::FaceMakerBullseye
  LengthFwd = 2
  LengthRev = 0
  Solid = true
  Symmetric = false
FEATURE [Part::Extrusion] Extrude194
  Base = -> path34096_9_4_8_5_9_93
  Dir = (0,0,1)
  DirMode = 0
  FaceMakerClass = Part::FaceMakerBullseye
  LengthFwd = 2
  LengthRev = 0
  Solid = true
  Symmetric = false
FEATURE [Part::Extrusion] Extrude195
  Base = -> path34072_1_9_5_5_4_3_8
  Dir = (0,0,1)
  DirMode = 0
  FaceMakerClass = Part::FaceMakerBullseye
  LengthFwd = 2
  LengthRev = 0
  Solid = true
  Symmetric = false
FEATURE [Part::Extrusion] Extrude196
  Base = -> path34070_8_0_8_3_8_7
  Dir = (0,0,1)
  DirMode = 0
  FaceMakerClass = Part::FaceMakerBullseye
  LengthFwd = 2
  LengthRev = 0
  Solid = true
  Symmetric = false
FEATURE [Part::Extrusion] Extrude197
  Base = -> path52377_0_5_0_4_2_41_0_0_5_6_1_7_0_4
  Dir = (0,0,1)
  DirMode = 0
  FaceMakerClass = Part::FaceMakerBullseye
  LengthFwd = 2
  LengthRev = 0
  Solid = true
  Symmetric = false
FEATURE [Part::Extrusion] Extrude198
  Base = -> path34096_2_0_0_4_9_0
  Dir = (0,0,1)
  DirMode = 0
  FaceMakerClass = Part::FaceMakerBullseye
  LengthFwd = 2
  LengthRev = 0
  Solid = true
  Symmetric = false
FEATURE [Part::Extrusion] Extrude199
  Base = -> path34096_9_5_75_3_1
  Dir = (0,0,1)
  DirMode = 0
  FaceMakerClass = Part::FaceMakerBullseye
  LengthFwd = 2
  LengthRev = 0
  Solid = true
  Symmetric = false
FEATURE [Part::Extrusion] Extrude200
  Base = -> path34072_1_9_51_8_3_7
  Dir = (0,0,1)
  DirMode = 0
  FaceMakerClass = Part::FaceMakerBullseye
  LengthFwd = 2
  LengthRev = 0
  Solid = true
  Symmetric = false
FEATURE [Part::Extrusion] Extrude201
  Base = -> path34070_8_4_65_6_0
  Dir = (0,0,1)
  DirMode = 0
  FaceMakerClass = Part::FaceMakerBullseye
  LengthFwd = 2
  LengthRev = 0
  Solid = true
  Symmetric = false
FEATURE [Part::Extrusion] Extrude202
  Base = -> path52377_0_5_0_4_2_41_0_0_5_6_1_6_5_0_5
  Dir = (0,0,1)
  DirMode = 0
  FaceMakerClass = Part::FaceMakerBullseye
  LengthFwd = 2
  LengthRev = 0
  Solid = true
  Symmetric = false
FEATURE [Part::Extrusion] Extrude203
  Base = -> path34096_2_0_0_2_7_5_5
  Dir = (0,0,1)
  DirMode = 0
  FaceMakerClass = Part::FaceMakerBullseye
  LengthFwd = 2
  LengthRev = 0
  Solid = true
  Symmetric = false
FEATURE [Part::Extrusion] Extrude204
  Base = -> path34096_9_5_7_9_2_7
  Dir = (0,0,1)
  DirMode = 0
  FaceMakerClass = Part::FaceMakerBullseye
  LengthFwd = 2
  LengthRev = 0
  Solid = true
  Symmetric = false
FEATURE [Part::Extrusion] Extrude205
  Base = -> path34072_1_9_51_2_1_4_4
  Dir = (0,0,1)
  DirMode = 0
  FaceMakerClass = Part::FaceMakerBullseye
  LengthFwd = 2
  LengthRev = 0
  Solid = true
  Symmetric = false
FEATURE [Part::Extrusion] Extrude206
  Base = -> path34070_8_4_6_1_1_1
  Dir = (0,0,1)
  DirMode = 0
  FaceMakerClass = Part::FaceMakerBullseye
  LengthFwd = 2
  LengthRev = 0
  Solid = true
  Symmetric = false
FEATURE [Part::Extrusion] Extrude207
  Base = -> path52377_0_5_0_4_2_41_0_0_5_6_5_7_1_3_9
  Dir = (0,0,1)
  DirMode = 0
  FaceMakerClass = Part::FaceMakerBullseye
  LengthFwd = 2
  LengthRev = 0
  Solid = true
  Symmetric = false
FEATURE [Part::Extrusion] Extrude208
  Base = -> path34096_2_0_4_8_5_3_9
  Dir = (0,0,1)
  DirMode = 0
  FaceMakerClass = Part::FaceMakerBullseye
  LengthFwd = 2
  LengthRev = 0
  Solid = true
  Symmetric = false
FEATURE [Part::Extrusion] Extrude209
  Base = -> path34096_9_4_8_5_8_7
  Dir = (0,0,1)
  DirMode = 0
  FaceMakerClass = Part::FaceMakerBullseye
  LengthFwd = 2
  LengthRev = 0
  Solid = true
  Symmetric = false
FEATURE [Part::Extrusion] Extrude210
  Base = -> path34072_1_9_5_5_4_31_0
  Dir = (0,0,1)
  DirMode = 0
  FaceMakerClass = Part::FaceMakerBullseye
  LengthFwd = 2
  LengthRev = 0
  Solid = true
  Symmetric = false
FEATURE [Part::Extrusion] Extrude211
  Base = -> path34070_8_0_8_3_1_3
  Dir = (0,0,1)
  DirMode = 0
  FaceMakerClass = Part::FaceMakerBullseye
  LengthFwd = 2
  LengthRev = 0
  Solid = true
  Symmetric = false
FEATURE [Part::Extrusion] Extrude212
  Base = -> path52377_0_5_0_4_2_41_0_0_5_6_5_7_1_9_7_7
  Dir = (0,0,1)
  DirMode = 0
  FaceMakerClass = Part::FaceMakerBullseye
  LengthFwd = 2
  LengthRev = 0
  Solid = true
  Symmetric = false
FEATURE [Part::Extrusion] Extrude213
  Base = -> path34096_2_0_4_8_5_1_5_05
  Dir = (0,0,1)
  DirMode = 0
  FaceMakerClass = Part::FaceMakerBullseye
  LengthFwd = 2
  LengthRev = 0
  Solid = true
  Symmetric = false
FEATURE [Part::Extrusion] Extrude214
  Base = -> path34096_9_4_8_5_9_9_09
  Dir = (0,0,1)
  DirMode = 0
  FaceMakerClass = Part::FaceMakerBullseye
  LengthFwd = 2
  LengthRev = 0
  Solid = true
  Symmetric = false
FEATURE [Part::Extrusion] Extrude215
  Base = -> path34072_1_9_5_5_4_3_4_3
  Dir = (0,0,1)
  DirMode = 0
  FaceMakerClass = Part::FaceMakerBullseye
  LengthFwd = 2
  LengthRev = 0
  Solid = true
  Symmetric = false
FEATURE [Part::Extrusion] Extrude216
  Base = -> path34070_8_0_8_3_8_5_5
  Dir = (0,0,1)
  DirMode = 0
  FaceMakerClass = Part::FaceMakerBullseye
  LengthFwd = 2
  LengthRev = 0
  Solid = true
  Symmetric = false
FEATURE [Part::Extrusion] Extrude217
  Base = -> path52377_0_5_0_4_2_41_0_0_5_6_5_7_1_9_7_1_8
  Dir = (0,0,1)
  DirMode = 0
  FaceMakerClass = Part::FaceMakerBullseye
  LengthFwd = 2
  LengthRev = 0
  Solid = true
  Symmetric = false
FEATURE [Part::Extrusion] Extrude218
  Base = -> path34096_2_0_4_8_5_1_5_0_30
  Dir = (0,0,1)
  DirMode = 0
  FaceMakerClass = Part::FaceMakerBullseye
  LengthFwd = 2
  LengthRev = 0
  Solid = true
  Symmetric = false
FEATURE [Part::Extrusion] Extrude219
  Base = -> path34096_9_4_8_5_9_9_0_41
  Dir = (0,0,1)
  DirMode = 0
  FaceMakerClass = Part::FaceMakerBullseye
  LengthFwd = 2
  LengthRev = 0
  Solid = true
  Symmetric = false
FEATURE [Part::Extrusion] Extrude220
  Base = -> path34072_1_9_5_5_4_3_4_2_7
  Dir = (0,0,1)
  DirMode = 0
  FaceMakerClass = Part::FaceMakerBullseye
  LengthFwd = 2
  LengthRev = 0
  Solid = true
  Symmetric = false
FEATURE [Part::Extrusion] Extrude221
  Base = -> path34070_8_0_8_3_8_5_0_9
  Dir = (0,0,1)
  DirMode = 0
  FaceMakerClass = Part::FaceMakerBullseye
  LengthFwd = 2
  LengthRev = 0
  Solid = true
  Symmetric = false
FEATURE [Part::Extrusion] Extrude222
  Base = -> path52377_0_5_0_4_2_41_0_0_5_6_5_7_1_9_7_1_9_3
  Dir = (0,0,1)
  DirMode = 0
  FaceMakerClass = Part::FaceMakerBullseye
  LengthFwd = 2
  LengthRev = 0
  Solid = true
  Symmetric = false
FEATURE [Part::Extrusion] Extrude223
  Base = -> path34096_2_0_4_8_5_1_5_0_3_2
  Dir = (0,0,1)
  DirMode = 0
  FaceMakerClass = Part::FaceMakerBullseye
  LengthFwd = 2
  LengthRev = 0
  Solid = true
  Symmetric = false
FEATURE [Part::Extrusion] Extrude224
  Base = -> path34096_9_4_8_5_9_9_0_4_9
  Dir = (0,0,1)
  DirMode = 0
  FaceMakerClass = Part::FaceMakerBullseye
  LengthFwd = 2
  LengthRev = 0
  Solid = true
  Symmetric = false
FEATURE [Part::Extrusion] Extrude225
  Base = -> path34072_1_9_5_5_4_3_4_2_6_9
  Dir = (0,0,1)
  DirMode = 0
  FaceMakerClass = Part::FaceMakerBullseye
  LengthFwd = 2
  LengthRev = 0
  Solid = true
  Symmetric = false
FEATURE [Part::Extrusion] Extrude226
  Base = -> path34070_8_0_8_3_8_5_0_4_8
  Dir = (0,0,1)
  DirMode = 0
  FaceMakerClass = Part::FaceMakerBullseye
  LengthFwd = 2
  LengthRev = 0
  Solid = true
  Symmetric = false
FEATURE [Part::Extrusion] Extrude227
  Base = -> path52377_0_5_0_4_2_41_0_0_5_6_5_7_1_9_7_1_1_8
  Dir = (0,0,1)
  DirMode = 0
  FaceMakerClass = Part::FaceMakerBullseye
  LengthFwd = 2
  LengthRev = 0
  Solid = true
  Symmetric = false
FEATURE [Part::Extrusion] Extrude228
  Base = -> path34096_2_0_4_8_5_1_5_0_5_9
  Dir = (0,0,1)
  DirMode = 0
  FaceMakerClass = Part::FaceMakerBullseye
  LengthFwd = 2
  LengthRev = 0
  Solid = true
  Symmetric = false
FEATURE [Part::Extrusion] Extrude229
  Base = -> path34096_9_4_8_5_9_9_0_8_7
  Dir = (0,0,1)
  DirMode = 0
  FaceMakerClass = Part::FaceMakerBullseye
  LengthFwd = 2
  LengthRev = 0
  Solid = true
  Symmetric = false
FEATURE [Part::Extrusion] Extrude230
  Base = -> path34072_1_9_5_5_4_3_4_2_3_0
  Dir = (0,0,1)
  DirMode = 0
  FaceMakerClass = Part::FaceMakerBullseye
  LengthFwd = 2
  LengthRev = 0
  Solid = true
  Symmetric = false
FEATURE [Part::Extrusion] Extrude231
  Base = -> path34070_8_0_8_3_8_5_0_7_8
  Dir = (0,0,1)
  DirMode = 0
  FaceMakerClass = Part::FaceMakerBullseye
  LengthFwd = 2
  LengthRev = 0
  Solid = true
  Symmetric = false
FEATURE [Part::Extrusion] Extrude232
  Base = -> path37937_8_6
  Dir = (0,0,1)
  DirMode = 0
  FaceMakerClass = Part::FaceMakerBullseye
  LengthFwd = 2
  LengthRev = 0
  Solid = true
  Symmetric = false
FEATURE [Part::Extrusion] Extrude233
  Base = -> path37931_6_7
  Dir = (0,0,1)
  DirMode = 0
  FaceMakerClass = Part::FaceMakerBullseye
  LengthFwd = 2
  LengthRev = 0
  Solid = true
  Symmetric = false
FEATURE [Part::Extrusion] Extrude234
  Base = -> path37321_9_5
  Dir = (0,0,1)
  DirMode = 0
  FaceMakerClass = Part::FaceMakerBullseye
  LengthFwd = 2
  LengthRev = 0
  Solid = true
  Symmetric = false
FEATURE [Part::Extrusion] Extrude235
  Base = -> path37327_3_6
  Dir = (0,0,1)
  DirMode = 0
  FaceMakerClass = Part::FaceMakerBullseye
  LengthFwd = 2
  LengthRev = 0
  Solid = true
  Symmetric = false
FEATURE [Part::Extrusion] Extrude236
  Base = -> path37329_6_1
  Dir = (0,0,1)
  DirMode = 0
  FaceMakerClass = Part::FaceMakerBullseye
  LengthFwd = 2
  LengthRev = 0
  Solid = true
  Symmetric = false
FEATURE [Part::Extrusion] Extrude237
  Base = -> path37333_00_0
  Dir = (0,0,1)
  DirMode = 0
  FaceMakerClass = Part::FaceMakerBullseye
  LengthFwd = 2
  LengthRev = 0
  Solid = true
  Symmetric = false
FEATURE [Part::Extrusion] Extrude238
  Base = -> circle37301_1_8
  Dir = (0,0,1)
  DirMode = 0
  FaceMakerClass = Part::FaceMakerBullseye
  LengthFwd = 2
  LengthRev = 0
  Solid = true
  Symmetric = false
FEATURE [Part::Extrusion] Extrude239
  Base = -> circle37295_7_4
  Dir = (0,0,1)
  DirMode = 0
  FaceMakerClass = Part::FaceMakerBullseye
  LengthFwd = 2
  LengthRev = 0
  Solid = true
  Symmetric = false
FEATURE [Part::Extrusion] Extrude240
  Base = -> rect117948_11_2
  Dir = (0,0,1)
  DirMode = 0
  FaceMakerClass = Part::FaceMakerBullseye
  LengthFwd = 2
  LengthRev = 0
  Solid = true
  Symmetric = false
FEATURE [Part::Extrusion] Extrude241
  Base = -> rect117948_2_00_4
  Dir = (0,0,1)
  DirMode = 0
  FaceMakerClass = Part::FaceMakerBullseye
  LengthFwd = 2
  LengthRev = 0
  Solid = true
  Symmetric = false
FEATURE [Part::MultiFuse] Fusion002  label="wells_right"
  Placement = pos=(0,0,1) rot=(0,0,1;0rad)
  Shapes = -> [Extrude127,Extrude128,Extrude129,Extrude130,Extrude131,Extrude132,Extrude133,Extrude134,Extrude135,Extrude136,Extrude137,Extrude138,Extrude139,Extrude140,Extrude141,Extrude142,Extrude143,Extrude144,Extrude145,Extrude146,Extrude147,Extrude148,Extrude149,Extrude150,Extrude151,Extrude152,Extrude153,Extrude154,Extrude155,Extrude156,Extrude157,Extrude158,Extrude159,Extrude160,Extrude161,Extrude162,+79 more]
FEATURE [Part::FeaturePython] XOR004  label="right"  # WARN: FeaturePython — macro-defined, semantics opaque (R4)
  Objects = -> [Part__Mirroring,Fusion002]
  Placement = pos=(140,90,0) rot=(0,0,1;0rad)
  Tolerance = 0
